FCSTD DOCUMENT  (FreeCAD 0.19RUnknown)
Label: Case-3RF-1DC
License: All rights reserved
LicenseURL: http://en.wikipedia.org/wiki/All_rights_reserved
objects: Part::FeaturePython×54, App::Part×36, Part::Feature×33, Sketcher::SketchObject×20, PartDesign::Boolean×13, PartDesign::Pocket×10, PartDesign::Pad×8, PartDesign::Body×3, PartDesign::AdditiveLoft×1
note: 161 computed .brp shape members not serialized (recipe doc carries the construction recipe); baked Part::Feature solids carry a one-line shape summary decoded from their .brp

FEATURE [Part::Feature] Part__Feature  label="SOLID"
  shape: bbox 3 x 3 x 0.52 mm, 110 faces (baked)
FEATURE [App::Part] UQFN_16_1EP_3x3mm_P0_5mm_EP1_75x1_75mm  label="UQFN-16-1EP_3x3mm_P0.5mm_EP1.75x1.75mm"
  Group = -> [Part__Feature]
  Origin = -> Origin
  Placement = pos=(150,-94,1.65) rot=(0,0,1;0rad)
FEATURE [Part::Feature] Part__Feature001  label="COMPOUND"
  shape: bbox 6.008 x 15.88 x 9.525 mm, 27 faces (baked)
FEATURE [Part::Feature] Part__Feature002  label="COMPOUND001"
  shape: bbox 2.61 x 2.61 x 7.92 mm, 9 faces (baked)
FEATURE [App::Part] COMPOUND  label="COMPOUND002"
  Group = -> [Part__Feature001,Part__Feature002]
  Origin = -> Origin001
FEATURE [App::Part] _42_1701_626  label="142-1701-626"
  Group = -> [COMPOUND]
  Origin = -> Origin002
  Placement = pos=(166.9,-93.75,1.85) rot=(0,1,0;1.5708rad)
FEATURE [Part::Feature] Part__Feature003  label="COMPOUND003"
  shape: bbox 6.008 x 15.88 x 9.525 mm, 27 faces (baked)
FEATURE [Part::Feature] Part__Feature004  label="COMPOUND004"
  shape: bbox 2.61 x 2.61 x 7.92 mm, 9 faces (baked)
FEATURE [App::Part] COMPOUND001  label="COMPOUND005"
  Group = -> [Part__Feature003,Part__Feature004]
  Origin = -> Origin003
FEATURE [App::Part] _42_1701_626001  label="142-1701-627"
  Group = -> [COMPOUND001]
  Origin = -> Origin004
  Placement = pos=(133.1,-93.75,1.85) rot=(-0.707107,0,0.707107;3.14159rad)
FEATURE [Part::Feature] Part__Feature005  label="COMPOUND006"
  shape: bbox 6.008 x 16 x 16.53 mm, 35 faces (baked)
FEATURE [App::Part] _32147_48  label="132147-48"
  Group = -> [Part__Feature005]
  Origin = -> Origin005
  Placement = pos=(150,-74.95,2.25) rot=(-0.57735,0.57735,0.57735;2.0944rad)
FEATURE [Part::Feature] Part__Feature006  label="SOLID001"
  shape: bbox 1 x 0.5 x 0.5 mm, 28 faces (baked)
FEATURE [App::Part] C_0402_1005Metric
  Group = -> [Part__Feature006]
  Origin = -> Origin006
  Placement = pos=(155.685,-89.7,1.65) rot=(0,0,1;0rad)
FEATURE [Part::Feature] Part__Feature007  label="SOLID002"
  shape: bbox 1 x 0.5 x 0.5 mm, 28 faces (baked)
FEATURE [App::Part] C_0402_1005Metric001
  Group = -> [Part__Feature007]
  Origin = -> Origin007
  Placement = pos=(155.685,-88.7,1.65) rot=(0,0,1;0rad)
FEATURE [Part::Feature] Part__Feature008  label="SOLID003"
  shape: bbox 1 x 0.5 x 0.5 mm, 28 faces (baked)
FEATURE [App::Part] C_0402_1005Metric002
  Group = -> [Part__Feature008]
  Origin = -> Origin008
  Placement = pos=(149.735,-88.175,1.65) rot=(0,0,1;0rad)
FEATURE [Part::Feature] Part__Feature009  label="SOLID004"
  shape: bbox 1 x 0.5 x 0.5 mm, 28 faces (baked)
FEATURE [App::Part] C_0402_1005Metric003
  Group = -> [Part__Feature009]
  Origin = -> Origin009
  Placement = pos=(149.735,-89.25,1.65) rot=(0,0,1;0rad)
FEATURE [Part::Feature] Part__Feature010  label="SOLID005"
  shape: bbox 1.6 x 0.8 x 0.8 mm, 28 faces (baked)
FEATURE [App::Part] C_0603_1608Metric
  Group = -> [Part__Feature010]
  Origin = -> Origin010
  Placement = pos=(154.787,-85.5,1.65) rot=(0,0,1;0rad)
FEATURE [Part::Feature] Part__Feature011  label="SOLID006"
  shape: bbox 1 x 0.5 x 0.5 mm, 28 faces (baked)
FEATURE [App::Part] L_0402_1005Metric
  Group = -> [Part__Feature011]
  Origin = -> Origin011
  Placement = pos=(149.25,-90.79,1.65) rot=(0,0,1;1.5708rad)
FEATURE [Part::Feature] Part__Feature012  label="SOLID007"
  shape: bbox 1.6 x 0.8 x 0.8 mm, 28 faces (baked)
FEATURE [App::Part] L_0603_1608Metric
  Group = -> [Part__Feature012]
  Origin = -> Origin012
  Placement = pos=(152.988,-91,1.65) rot=(0,0,1;0rad)
FEATURE [Part::Feature] Part__Feature013  label="SOLID008"
  shape: bbox 1 x 0.5 x 0.35 mm, 26 faces (baked)
FEATURE [App::Part] R_0402_1005Metric
  Group = -> [Part__Feature013]
  Origin = -> Origin013
  Placement = pos=(155.2,-87.2,1.65) rot=(0,0,1;1.5708rad)
FEATURE [Part::Feature] Part__Feature014  label="SOLID009"
  shape: bbox 1 x 0.5 x 0.35 mm, 26 faces (baked)
FEATURE [App::Part] R_0402_1005Metric001
  Group = -> [Part__Feature014]
  Origin = -> Origin014
  Placement = pos=(149.25,-86.65,1.65) rot=(0,0,-1;1.5708rad)
FEATURE [Part::Feature] Part__Feature015  label="SOLID010"
  shape: bbox 1 x 0.5 x 0.5 mm, 28 faces (baked)
FEATURE [App::Part] C_0402_1005Metric004
  Group = -> [Part__Feature015]
  Origin = -> Origin015
  Placement = pos=(158.265,-93.75,1.65) rot=(0,0,1;0rad)
FEATURE [Part::Feature] Part__Feature016  label="SOLID011"
  shape: bbox 1 x 0.5 x 0.35 mm, 26 faces (baked)
FEATURE [App::Part] R_0402_1005Metric002
  Group = -> [Part__Feature016]
  Origin = -> Origin016
  Placement = pos=(153.155,-93.75,1.65) rot=(0,0,1;3.14159rad)
FEATURE [Part::Feature] Part__Feature017  label="SOLID012"
  shape: bbox 1 x 0.5 x 0.35 mm, 26 faces (baked)
FEATURE [App::Part] R_0402_1005Metric003
  Group = -> [Part__Feature017]
  Origin = -> Origin017
  Placement = pos=(154.57,-94.235,1.65) rot=(0,0,1;1.5708rad)
FEATURE [Part::Feature] Part__Feature018  label="SOLID013"
  shape: bbox 1 x 0.5 x 0.5 mm, 28 faces (baked)
FEATURE [App::Part] C_0402_1005Metric005
  Group = -> [Part__Feature018]
  Origin = -> Origin018
  Placement = pos=(142.63,-94.235,1.65) rot=(0,0,1;1.5708rad)
FEATURE [Part::Feature] Part__Feature019  label="SOLID014"
  shape: bbox 1 x 0.5 x 0.5 mm, 28 faces (baked)
FEATURE [App::Part] C_0402_1005Metric006
  Group = -> [Part__Feature019]
  Origin = -> Origin019
  Placement = pos=(146.835,-93.75,1.65) rot=(0,0,1;0rad)
FEATURE [Part::Feature] Part__Feature020  label="SOLID015"
  shape: bbox 1 x 0.5 x 0.5 mm, 28 faces (baked)
FEATURE [App::Part] L_0402_1005Metric001
  Group = -> [Part__Feature020]
  Origin = -> Origin020
  Placement = pos=(144.03,-93.75,1.65) rot=(0,0,1;3.14159rad)
FEATURE [Part::Feature] Part__Feature021  label="SOLID016"
  shape: bbox 1 x 0.5 x 0.5 mm, 28 faces (baked)
FEATURE [App::Part] L_0402_1005Metric002
  Group = -> [Part__Feature021]
  Origin = -> Origin021
  Placement = pos=(145.43,-94.235,1.65) rot=(0,0,-1;1.5708rad)
FEATURE [Part::Feature] Part__Feature022  label="COMPOUND007"
  shape: bbox 30 x 30 x 1.6 mm, 14 faces (baked)
FEATURE [App::Part] Open_CASCADE_STEP_translator_6_9_1  label="Open CASCADE STEP translator 6.9 1"
  Group = -> [UQFN_16_1EP_3x3mm_P0_5mm_EP1_75x1_75mm,_42_1701_626,_42_1701_626001,_32147_48,C_0402_1005Metric,C_0402_1005Metric001,C_0402_1005Metric002,C_0402_1005Metric003,C_0603_1608Metric,L_0402_1005Metric,L_0603_1608Metric,R_0402_1005Metric,R_0402_1005Metric001,C_0402_1005Metric004,R_0402_1005Metric002,R_0402_1005Metric003,C_0402_1005Metric005,C_0402_1005Metric006,L_0402_1005Metric001,L_0402_1005Metric002,+1 more]
  Origin = -> Origin022
  Placement = pos=(-139,83,0) rot=(0,0,1;0rad)
FEATURE [Sketcher::SketchObject] Sketch
  FullyConstrained = true
  MapMode = 5
  Support = -> [XY_Plane023]
  sketch-geometry (32):
    g0: LineSegment StartX=23 StartY=8.05 StartZ=0 EndX=-1 EndY=8.05 EndZ=0
    g1: LineSegment StartX=-5.85 StartY=1 StartZ=0 EndX=-5.85 EndY=-23 EndZ=0
    g2: LineSegment StartX=-1 StartY=-27.85 StartZ=0 EndX=23 EndY=-27.85 EndZ=0
    g3: LineSegment StartX=27.85 StartY=-23 StartZ=0 EndX=27.85 EndY=1 EndZ=0
    g4: ArcOfCircle CenterX=23 CenterY=10.05 CenterZ=0 NormalX=0 NormalY=0 NormalZ=1 AngleXU=0 Radius=2 StartAngle=4.71239 EndAngle=6.28319
    g5: ArcOfCircle CenterX=29.85 CenterY=1 CenterZ=0 NormalX=0 NormalY=0 NormalZ=1 AngleXU=0 Radius=2 StartAngle=1.5708 EndAngle=3.14159
    g6: ArcOfCircle CenterX=-7.85 CenterY=-23 CenterZ=0 NormalX=0 NormalY=0 NormalZ=1 AngleXU=0 Radius=2 StartAngle=4.71239 EndAngle=6.28319
    g7: ArcOfCircle CenterX=-1 CenterY=-29.85 CenterZ=0 NormalX=0 NormalY=0 NormalZ=1 AngleXU=0 Radius=2 StartAngle=1.5708 EndAngle=3.14159
    g8: ArcOfCircle CenterX=23 CenterY=-29.85 CenterZ=0 NormalX=0 NormalY=0 NormalZ=1 AngleXU=0 Radius=2 StartAngle=0 EndAngle=1.5708
    g9: ArcOfCircle CenterX=29.85 CenterY=-23 CenterZ=0 NormalX=0 NormalY=0 NormalZ=1 AngleXU=0 Radius=2 StartAngle=3.14159 EndAngle=4.71239
    g10: ArcOfCircle CenterX=-1 CenterY=10.05 CenterZ=0 NormalX=0 NormalY=0 NormalZ=1 AngleXU=0 Radius=2 StartAngle=3.14159 EndAngle=4.71239
    g11: ArcOfCircle CenterX=-7.85 CenterY=1 CenterZ=0 NormalX=0 NormalY=0 NormalZ=1 AngleXU=0 Radius=2 StartAngle=0 EndAngle=1.5708
    g12: LineSegment StartX=25 StartY=10.05 StartZ=0 EndX=25 EndY=16 EndZ=0
    g13: LineSegment StartX=25 StartY=16 StartZ=0 EndX=38 EndY=16 EndZ=0
    g14: LineSegment StartX=38 StartY=16 StartZ=0 EndX=38 EndY=3 EndZ=0
    g15: LineSegment StartX=29.85 StartY=3 StartZ=0 EndX=38 EndY=3 EndZ=0
    g16: LineSegment StartX=-7.85 StartY=-25 StartZ=0 EndX=-16 EndY=-25 EndZ=0
    g17: LineSegment StartX=-16 StartY=-25 StartZ=0 EndX=-16 EndY=-38 EndZ=0
    g18: LineSegment StartX=-16 StartY=-38 StartZ=0 EndX=-3 EndY=-38 EndZ=0
    g19: LineSegment StartX=-3 StartY=-29.85 StartZ=0 EndX=-3 EndY=-38 EndZ=0
    g20: LineSegment StartX=29.85 StartY=-25 StartZ=0 EndX=38 EndY=-25 EndZ=0
    g21: LineSegment StartX=38 StartY=-25 StartZ=0 EndX=38 EndY=-38 EndZ=0
    g22: LineSegment StartX=38 StartY=-38 StartZ=0 EndX=25 EndY=-38 EndZ=0
    g23: LineSegment StartX=25 StartY=-38 StartZ=0 EndX=25 EndY=-29.85 EndZ=0
    g24: LineSegment StartX=-3 StartY=10.05 StartZ=0 EndX=-3 EndY=16 EndZ=0
    g25: LineSegment StartX=-3 StartY=16 StartZ=0 EndX=-16 EndY=16 EndZ=0
    g26: LineSegment StartX=-16 StartY=16 StartZ=0 EndX=-16 EndY=3 EndZ=0
    g27: LineSegment StartX=-7.85 StartY=3 StartZ=0 EndX=-16 EndY=3 EndZ=0
    g28: GeomPoint X=31.5 Y=9.5 Z=0
    g29: GeomPoint X=-9.5 Y=9.5 Z=0
    g30: GeomPoint X=-9.5 Y=-32.5 Z=0
    g31: GeomPoint X=31.5 Y=-32.5 Z=0
  constraints (98):
    c: Horizontal(g0)
    c: Horizontal(g2)
    c: Vertical(g1)
    c: Vertical(g3)
    c: Equal(g6,g7)
    c: Equal(g7,g8)
    c: Equal(g8,g9)
    c: Equal(g9,g5)
    c: Equal(g5,g4)
    c: Equal(g4,g10)
    c: Equal(g10,g11)
    c: Vertical(g8,g8)
    c: Vertical(g8,g4)
    c: Vertical(g4,g4)
    c: Horizontal(g9,g9)
    c: Horizontal(g9,g6)
    c: Horizontal(g6,g6)
    c: Horizontal(g11,g11)
    c: Horizontal(g11,g5)
    c: Horizontal(g5,g5)
    c: Vertical(g10,g10)
    c: Vertical(g10,g7)
    c: Vertical(g7,g7)
    c: Coincident(g0,g10)
    c: Coincident(g2,g7)
    c: Coincident(g6,g1)
    c: Horizontal(g7,g7)
    c: Horizontal(g8,g8)
    c: Coincident(g9,g3)
    c: Vertical(g6,g6)
    c: Vertical(g11,g11)
    c: Vertical(g9,g9)
    c: Vertical(g5,g5)
    c: Coincident(g0,g4)
    c: Horizontal(g10,g10)
    c: Horizontal(g4,g4)
    c: Coincident(g5,g3)
    c: Coincident(g1,g11)
    c: Coincident(g12,g4)
    c: Vertical(g12)
    c: Coincident(g13,g12)
    c: Horizontal(g13)
    c: Coincident(g14,g13)
    c: Vertical(g14)
    c: Coincident(g15,g5)
    c: Coincident(g15,g14)
    c: Horizontal(g15)
    c: Equal(g13,g14)
    c: DistanceX(g13,g13) = 13
    c: Coincident(g16,g6)
    c: Horizontal(g16)
    c: Coincident(g17,g16)
    c: Vertical(g17)
    c: Coincident(g18,g17)
    c: Horizontal(g18)
    c: Coincident(g19,g7)
    c: Coincident(g19,g18)
    c: Vertical(g19)
    c: Equal(g17,g18)
    c: Equal(g18,g14)
    c: Equal(g16,g19)
    c: Equal(g19,g15)
    c: Coincident(g20,g9)
    c: Horizontal(g20)
    c: Coincident(g21,g20)
    c: Vertical(g21)
    c: Coincident(g22,g21)
    c: Horizontal(g22)
    c: Coincident(g23,g22)
    c: Coincident(g23,g8)
    c: Vertical(g23)
    c: Equal(g14,g21)
    c: Equal(g21,g22)
    c: Coincident(g24,g10)
    c: Vertical(g24)
    c: Coincident(g25,g24)
    c: Horizontal(g25)
    c: Coincident(g26,g25)
    c: Vertical(g26)
    c: Coincident(g27,g11)
    c: Coincident(g27,g26)
    c: Horizontal(g27)
    c: DistanceX(g0,g0) = 24
    c: DistanceX(g1,g-1) = 5.85
    c: Radius(g10) = 2
    c: Coincident(g2,g8)
    c: DistanceX(g-1,g0) = -1
    c: DistanceY(g2,g-1) = 27.85
    c: DistanceY(g-1,g0) = 8.05
    c: Horizontal(g13,g25)
    c: Vertical(g25,g17)
    c: Horizontal(g31,g30)
    c: Vertical(g29,g30)
    c: Vertical(g28,g31)
    c: Symmetric(g14,g12,g28)
    c: Symmetric(g24,g26,g29)
    c: DistanceY(g30,g6) = 7.5
    c: Equal(g0,g1)
FEATURE [Sketcher::SketchObject] Sketch006
  AttachmentOffset = pos=(0,0,7) rot=(0,0,1;0rad)
  ExternalGeometry = -> [Sketch]
  FullyConstrained = true
  MapMode = 2
  sketch-geometry (36):
    g0: ArcOfCircle CenterX=22 CenterY=-1.4e-15 CenterZ=0 NormalX=0 NormalY=0 NormalZ=1 AngleXU=0 Radius=4.2 StartAngle=0 EndAngle=1.5708
    g1: ArcOfCircle CenterX=-1.54e-14 CenterY=0 CenterZ=0 NormalX=0 NormalY=0 NormalZ=1 AngleXU=0 Radius=4.2 StartAngle=1.5708 EndAngle=3.14159
    g2: ArcOfCircle CenterX=-1.54e-14 CenterY=-22 CenterZ=0 NormalX=0 NormalY=0 NormalZ=1 AngleXU=0 Radius=4.2 StartAngle=3.14159 EndAngle=4.71239
    g3: ArcOfCircle CenterX=22 CenterY=-22 CenterZ=0 NormalX=0 NormalY=0 NormalZ=1 AngleXU=0 Radius=4.2 StartAngle=4.71239 EndAngle=6.28319
    g4: LineSegment StartX=-1.54e-14 StartY=4.2 StartZ=0 EndX=22 EndY=4.2 EndZ=0
    g5: LineSegment StartX=26.2 StartY=-1.4e-15 StartZ=0 EndX=26.2 EndY=-22 EndZ=0
    g6: LineSegment StartX=-4.2 StartY=-1.4e-15 StartZ=0 EndX=-4.2 EndY=-22 EndZ=0
    g7: LineSegment StartX=-1.54e-14 StartY=-26.2 StartZ=0 EndX=22 EndY=-26.2 EndZ=0
    g8: LineSegment StartX=27.85 StartY=1 StartZ=0 EndX=27.85 EndY=-23 EndZ=0
    g9: LineSegment StartX=23 StartY=-27.85 StartZ=0 EndX=-1 EndY=-27.85 EndZ=0
    g10: LineSegment StartX=-3 StartY=-38 StartZ=0 EndX=-16 EndY=-38 EndZ=0
    g11: LineSegment StartX=-16 StartY=-38 StartZ=0 EndX=-16 EndY=-25 EndZ=0
    g12: LineSegment StartX=-5.85 StartY=-23 StartZ=0 EndX=-5.85 EndY=1 EndZ=0
    g13: LineSegment StartX=-1 StartY=8.05 StartZ=0 EndX=23 EndY=8.05 EndZ=0
    g14: ArcOfCircle CenterX=29.85 CenterY=1 CenterZ=0 NormalX=0 NormalY=0 NormalZ=1 AngleXU=0 Radius=2 StartAngle=1.5708 EndAngle=3.14159
    g15: ArcOfCircle CenterX=23 CenterY=10.05 CenterZ=0 NormalX=0 NormalY=0 NormalZ=1 AngleXU=0 Radius=2 StartAngle=4.71239 EndAngle=6.28319
    g16: ArcOfCircle CenterX=-1 CenterY=10.05 CenterZ=0 NormalX=0 NormalY=0 NormalZ=1 AngleXU=0 Radius=2 StartAngle=3.14159 EndAngle=4.71239
    g17: ArcOfCircle CenterX=-7.85 CenterY=1 CenterZ=0 NormalX=0 NormalY=0 NormalZ=1 AngleXU=0 Radius=2 StartAngle=0 EndAngle=1.5708
    g18: ArcOfCircle CenterX=-7.85 CenterY=-23 CenterZ=0 NormalX=0 NormalY=0 NormalZ=1 AngleXU=0 Radius=2 StartAngle=4.71239 EndAngle=6.28319
    g19: ArcOfCircle CenterX=29.85 CenterY=-23 CenterZ=0 NormalX=0 NormalY=0 NormalZ=1 AngleXU=0 Radius=2 StartAngle=3.14159 EndAngle=4.71239
    g20: ArcOfCircle CenterX=23 CenterY=-29.85 CenterZ=0 NormalX=0 NormalY=0 NormalZ=1 AngleXU=0 Radius=2 StartAngle=-1.013e-13 EndAngle=1.5708
    g21: ArcOfCircle CenterX=-1 CenterY=-29.85 CenterZ=0 NormalX=0 NormalY=0 NormalZ=1 AngleXU=0 Radius=2 StartAngle=1.5708 EndAngle=3.14159
    g22: LineSegment StartX=25 StartY=16 StartZ=0 EndX=38 EndY=16 EndZ=0
    g23: LineSegment StartX=38 StartY=16 StartZ=0 EndX=38 EndY=3 EndZ=0
    g24: LineSegment StartX=38 StartY=3 StartZ=0 EndX=29.85 EndY=3 EndZ=0
    g25: LineSegment StartX=25 StartY=10.05 StartZ=0 EndX=25 EndY=16 EndZ=0
    g26: LineSegment StartX=-3 StartY=10.05 StartZ=0 EndX=-3 EndY=16 EndZ=0
    g27: LineSegment StartX=-3 StartY=16 StartZ=0 EndX=-16 EndY=16 EndZ=0
    g28: LineSegment StartX=-16 StartY=16 StartZ=0 EndX=-16 EndY=3 EndZ=0
    g29: LineSegment StartX=-16 StartY=3 StartZ=0 EndX=-7.85 EndY=3 EndZ=0
    g30: LineSegment StartX=-16 StartY=-25 StartZ=0 EndX=-7.85 EndY=-25 EndZ=0
    g31: LineSegment StartX=-3 StartY=-38 StartZ=0 EndX=-3 EndY=-29.85 EndZ=0
    g32: LineSegment StartX=25 StartY=-29.85 StartZ=0 EndX=25 EndY=-38 EndZ=0
    g33: LineSegment StartX=25 StartY=-38 StartZ=0 EndX=38 EndY=-38 EndZ=0
    g34: LineSegment StartX=38 StartY=-38 StartZ=0 EndX=38 EndY=-25 EndZ=0
    g35: LineSegment StartX=38 StartY=-25 StartZ=0 EndX=29.85 EndY=-25 EndZ=0
  constraints (96):
    c: Coincident(g5,g0)
    c: Coincident(g5,g3)
    c: Vertical(g5)
    c: Coincident(g6,g1)
    c: Coincident(g6,g2)
    c: Vertical(g6)
    c: Coincident(g7,g2)
    c: Coincident(g7,g3)
    c: Horizontal(g7)
    c: Radius(g1) = 4.2
    c: Horizontal(g0,g0)
    c: Horizontal(g0,g1)
    c: Vertical(g0,g0)
    c: Vertical(g0,g3)
    c: Vertical(g3,g3)
    c: Vertical(g2,g2)
    c: Vertical(g2,g1)
    c: Coincident(g4,g1)
    c: Horizontal(g4)
    c: Coincident(g0,g4)
    c: DistanceX(g1,g0) = 22
    c: DistanceY(g3,g0) = 22
    c: Horizontal(g2,g2)
    c: Equal(g3,g2)
    c: Equal(g2,g0)
    c: Coincident(g1,g-1)
    c: Coincident(g11,g10)
    c: Coincident(g14,g8)
    c: Coincident(g15,g13)
    c: Coincident(g16,g13)
    c: Coincident(g17,g12)
    c: Coincident(g18,g12)
    c: Coincident(g19,g8)
    c: Coincident(g20,g9)
    c: Coincident(g21,g9)
    c: Coincident(g23,g22)
    c: Coincident(g24,g23)
    c: Coincident(g24,g14)
    c: Coincident(g25,g15)
    c: Coincident(g25,g22)
    c: Coincident(g26,g16)
    c: Coincident(g27,g26)
    c: Coincident(g28,g27)
    c: Coincident(g29,g28)
    c: Coincident(g29,g17)
    c: Coincident(g30,g11)
    c: Coincident(g30,g18)
    c: Coincident(g31,g10)
    c: Coincident(g31,g21)
    c: Coincident(g32,g20)
    c: Coincident(g33,g32)
    c: Coincident(g34,g33)
    c: Coincident(g35,g34)
    c: Coincident(g35,g19)
    c: Vertical(g1,g1)
    c: Coincident(g9,g-22)
    c: Coincident(g21,g-19)
    c: Coincident(g-18,g10)
    c: Equal(g-19,g21)
    c: Coincident(g20,g-20)
    c: Coincident(g9,g-22)
    c: Coincident(g20,g-21)
    c: Horizontal(g-21,g20)
    c: Coincident(g32,g-21)
    c: Coincident(g34,g-5)
    c: Coincident(g19,g-9)
    c: Horizontal(g8,g-9)
    c: Coincident(g19,g-9)
    c: Coincident(g14,g-8)
    c: Coincident(g23,g-6)
    c: Horizontal(g8,g14)
    c: Coincident(g14,g-8)
    c: Coincident(g15,g-17)
    c: Coincident(g22,g-17)
    c: Coincident(g-16,g15)
    c: Vertical(g13,g15)
    c: Coincident(g16,g-14)
    c: Coincident(g26,g-13)
    c: Coincident(g16,g-14)
    c: Vertical(g13,g16)
    c: Coincident(g28,g-3)
    c: Coincident(g17,g-11)
    c: Horizontal(g12,g-11)
    c: Coincident(g17,g-11)
    c: Coincident(g18,g-10)
    c: Coincident(g12,g-12)
    c: Vertical(g18,g18)
    c: Coincident(g11,g-4)
    c: Vertical(g28)
    c: Vertical(g11)
    c: Horizontal(g10)
    c: Horizontal(g33)
    c: Vertical(g34)
    c: Vertical(g23)
    c: Horizontal(g22)
    c: Horizontal(g27)
FEATURE [PartDesign::Pad] Pad
  Direction = (1,1,1)
  Length = 5
  Length2 = 100
  Profile = -> Sketch
  Reversed = true
  Type = 0
FEATURE [PartDesign::Pad] Pad001
  BaseFeature = -> Pad
  Direction = (1,1,1)
  Length = 9
  Length2 = 100
  Profile = -> Sketch006
  Type = 0
FEATURE [Sketcher::SketchObject] Sketch007
  AttachmentOffset = pos=(0,0,8.5) rot=(0,0,1;0rad)
  ExternalGeometry = -> [Sketch,Sketch006]
  FullyConstrained = true
  MapMode = 5
  Placement = pos=(0,0,8.5) rot=(0,0,1;0rad)
  Support = -> [XY_Plane023]
  sketch-geometry (12):
    g0: LineSegment StartX=38 StartY=16 StartZ=0 EndX=-16 EndY=16 EndZ=0
    g1: LineSegment StartX=-16 StartY=16 StartZ=0 EndX=-16 EndY=-38 EndZ=0
    g2: LineSegment StartX=-16 StartY=-38 StartZ=0 EndX=38 EndY=-38 EndZ=0
    g3: LineSegment StartX=38 StartY=-38 StartZ=0 EndX=38 EndY=16 EndZ=0
    g4: ArcOfCircle CenterX=22 CenterY=-22 CenterZ=0 NormalX=0 NormalY=0 NormalZ=1 AngleXU=0 Radius=4.2 StartAngle=4.71239 EndAngle=6.28319
    g5: ArcOfCircle CenterX=22 CenterY=-6e-16 CenterZ=0 NormalX=0 NormalY=0 NormalZ=1 AngleXU=0 Radius=4.2 StartAngle=0 EndAngle=1.5708
    g6: ArcOfCircle CenterX=0 CenterY=0 CenterZ=0 NormalX=0 NormalY=0 NormalZ=1 AngleXU=0 Radius=4.2 StartAngle=1.5708 EndAngle=3.14159
    g7: ArcOfCircle CenterX=-8e-16 CenterY=-22 CenterZ=0 NormalX=0 NormalY=0 NormalZ=1 AngleXU=0 Radius=4.2 StartAngle=3.14159 EndAngle=4.71239
    g8: LineSegment StartX=22 StartY=4.2 StartZ=0 EndX=0 EndY=4.2 EndZ=0
    g9: LineSegment StartX=-4.2 StartY=-1.4e-15 StartZ=0 EndX=-4.2 EndY=-22 EndZ=0
    g10: LineSegment StartX=-1.6e-15 StartY=-26.2 StartZ=0 EndX=22 EndY=-26.2 EndZ=0
    g11: LineSegment StartX=26.2 StartY=-22 StartZ=0 EndX=26.2 EndY=0 EndZ=0
  constraints (30):
    c: Coincident(g0,g1)
    c: Coincident(g1,g2)
    c: Coincident(g2,g3)
    c: Coincident(g3,g0)
    c: Horizontal(g0)
    c: Horizontal(g2)
    c: Vertical(g1)
    c: Vertical(g3)
    c: Coincident(g0,g-3)
    c: Coincident(g1,g-5)
    c: Coincident(g4,g-10)
    c: Coincident(g4,g-10)
    c: Coincident(g4,g-10)
    c: Coincident(g5,g-7)
    c: Coincident(g5,g-7)
    c: Coincident(g5,g-7)
    c: Coincident(g6,g-1)
    c: Coincident(g6,g-9)
    c: Coincident(g6,g-9)
    c: Coincident(g7,g-8)
    c: Coincident(g7,g-8)
    c: Coincident(g7,g-8)
    c: Coincident(g8,g5)
    c: Coincident(g8,g6)
    c: Coincident(g9,g6)
    c: Coincident(g9,g7)
    c: Coincident(g10,g7)
    c: Coincident(g10,g4)
    c: Coincident(g11,g4)
    c: Coincident(g11,g5)
FEATURE [PartDesign::Pad] Pad002
  BaseFeature = -> Pad001
  Direction = (1,1,1)
  Length = 3.5
  Length2 = 100
  Profile = -> Sketch007
  Type = 0
FEATURE [Sketcher::SketchObject] Sketch008
  AttachmentOffset = pos=(0,0,12) rot=(0,0,1;0rad)
  ExternalGeometry = -> [Sketch007]
  FullyConstrained = true
  MapMode = 5
  Placement = pos=(0,0,12) rot=(0,0,1;0rad)
  Support = -> [XY_Plane023]
  sketch-geometry (16):
    g0: ArcOfCircle CenterX=22 CenterY=-6e-16 CenterZ=0 NormalX=0 NormalY=0 NormalZ=1 AngleXU=0 Radius=5.5 StartAngle=1e-16 EndAngle=1.5708
    g1: ArcOfCircle CenterX=22 CenterY=-6e-16 CenterZ=0 NormalX=0 NormalY=0 NormalZ=1 AngleXU=0 Radius=8.5 StartAngle=1e-16 EndAngle=1.5708
    g2: ArcOfCircle CenterX=0 CenterY=0 CenterZ=0 NormalX=0 NormalY=0 NormalZ=1 AngleXU=0 Radius=5.5 StartAngle=1.5708 EndAngle=3.14159
    g3: ArcOfCircle CenterX=0 CenterY=0 CenterZ=0 NormalX=0 NormalY=0 NormalZ=1 AngleXU=0 Radius=8.5 StartAngle=1.5708 EndAngle=3.14159
    g4: LineSegment StartX=5e-16 StartY=8.5 StartZ=0 EndX=22 EndY=8.5 EndZ=0
    g5: LineSegment StartX=3e-16 StartY=5.5 StartZ=0 EndX=22 EndY=5.5 EndZ=0
    g6: ArcOfCircle CenterX=22 CenterY=-22 CenterZ=0 NormalX=0 NormalY=0 NormalZ=1 AngleXU=0 Radius=5.5 StartAngle=4.71239 EndAngle=6.28319
    g7: ArcOfCircle CenterX=22 CenterY=-22 CenterZ=0 NormalX=0 NormalY=0 NormalZ=1 AngleXU=0 Radius=8.5 StartAngle=4.71239 EndAngle=6.28319
    g8: ArcOfCircle CenterX=-5.8e-15 CenterY=-22 CenterZ=0 NormalX=0 NormalY=0 NormalZ=1 AngleXU=0 Radius=5.5 StartAngle=3.14159 EndAngle=4.71239
    g9: ArcOfCircle CenterX=-5.8e-15 CenterY=-22 CenterZ=0 NormalX=0 NormalY=0 NormalZ=1 AngleXU=0 Radius=8.5 StartAngle=3.14159 EndAngle=4.71239
    g10: LineSegment StartX=-5.5 StartY=-22 StartZ=0 EndX=-5.5 EndY=0 EndZ=0
    g11: LineSegment StartX=-8.5 StartY=1e-15 StartZ=0 EndX=-8.5 EndY=-22 EndZ=0
    g12: LineSegment StartX=-5.8e-15 StartY=-27.5 StartZ=0 EndX=22 EndY=-27.5 EndZ=0
    g13: LineSegment StartX=-7.4e-15 StartY=-30.5 StartZ=0 EndX=22 EndY=-30.5 EndZ=0
    g14: LineSegment StartX=27.5 StartY=-22 StartZ=0 EndX=27.5 EndY=0 EndZ=0
    g15: LineSegment StartX=30.5 StartY=3e-16 StartZ=0 EndX=30.5 EndY=-22 EndZ=0
  constraints (49):
    c: Coincident(g0,g-7)
    c: PointOnObject(g0,g-1)
    c: Coincident(g1,g0)
    c: PointOnObject(g1,g-1)
    c: PointOnObject(g2,g-2)
    c: PointOnObject(g2,g-1)
    c: PointOnObject(g3,g-2)
    c: PointOnObject(g3,g-1)
    c: Coincident(g4,g3)
    c: Coincident(g4,g1)
    c: Horizontal(g4)
    c: Tangent(g4,g1)
    c: Coincident(g5,g2)
    c: Coincident(g5,g0)
    c: Horizontal(g5)
    c: Coincident(g6,g-8)
    c: Coincident(g7,g6)
    c: PointOnObject(g9,g-2)
    c: Coincident(g10,g8)
    c: Coincident(g10,g2)
    c: Vertical(g10)
    c: Coincident(g11,g3)
    c: Coincident(g11,g9)
    c: Vertical(g11)
    c: Coincident(g12,g8)
    c: Coincident(g12,g6)
    c: Horizontal(g12)
    c: Coincident(g13,g9)
    c: Coincident(g13,g7)
    c: Horizontal(g13)
    c: Coincident(g14,g6)
    c: Coincident(g14,g0)
    c: Vertical(g14)
    c: Coincident(g15,g1)
    c: Coincident(g15,g7)
    c: Coincident(g3,g-1)
    c: Coincident(g2,g3)
    c: Vertical(g0,g1)
    c: Vertical(g6,g7)
    c: Vertical(g7,g6)
    c: Horizontal(g8,g9)
    c: Radius(g8) = 5.5
    c: Radius(g9) = 8.5
    c: Horizontal(g7,g6)
    c: Coincident(g8,g9)
    c: Coincident(g8,g-5)
    c: Vertical(g8,g8)
    c: Horizontal(g8,g8)
    c: DistanceX(g4,g4) = 22
FEATURE [PartDesign::Pocket] Pocket
  BaseFeature = -> Pad002
  Length = 2.8
  Length2 = 100
  Profile = -> Sketch008
  Type = 0
FEATURE [Part::FeaturePython] ScrewTap  label="M3x20.0-ScrewTap007"  # Fasteners workbench fastener (typed FeaturePython)
  Placement = pos=(0,0,10) rot=(0,0,1;0rad)
  diameter = 4
  invert = false
  length = 20
  matchOuter = true
  offset = 0
  thread = true
FEATURE [Part::FeaturePython] ScrewTap001  label="M3x20.0-ScrewTap006"  # Fasteners workbench fastener (typed FeaturePython)
  Placement = pos=(22,0,10) rot=(0,0,1;0rad)
  diameter = 4
  invert = false
  length = 20
  matchOuter = true
  offset = 0
  thread = true
FEATURE [Part::FeaturePython] ScrewTap002  label="M3x20.0-ScrewTap005"  # Fasteners workbench fastener (typed FeaturePython)
  Placement = pos=(22,-22,10) rot=(0,0,1;0rad)
  diameter = 4
  invert = false
  length = 20
  matchOuter = true
  offset = 0
  thread = true
FEATURE [Part::FeaturePython] ScrewTap003  label="M3x20.0-ScrewTap004"  # Fasteners workbench fastener (typed FeaturePython)
  Placement = pos=(0,-22,10) rot=(0,0,1;0rad)
  diameter = 4
  invert = false
  length = 20
  matchOuter = true
  offset = 0
  thread = true
FEATURE [Part::FeaturePython] ScrewTap004  label="M3x20.0-ScrewTap054"  # Fasteners workbench fastener (typed FeaturePython)
  Placement = pos=(-12,-34,12) rot=(0,0,1;0rad)
  diameter = 4
  invert = false
  length = 20
  matchOuter = true
  offset = 0
  thread = true
FEATURE [Part::FeaturePython] ScrewTap005  label="M3x20.0-ScrewTap055"  # Fasteners workbench fastener (typed FeaturePython)
  Placement = pos=(-12,12,12) rot=(0,0,1;0rad)
  diameter = 4
  invert = false
  length = 20
  matchOuter = true
  offset = 0
  thread = true
FEATURE [Part::FeaturePython] ScrewTap006  label="M3x20.0-ScrewTap056"  # Fasteners workbench fastener (typed FeaturePython)
  Placement = pos=(34,-34,12) rot=(0,0,1;0rad)
  diameter = 4
  invert = false
  length = 20
  matchOuter = true
  offset = 0
  thread = true
FEATURE [Part::FeaturePython] ScrewTap007  label="M3x20.0-ScrewTap"  # Fasteners workbench fastener (typed FeaturePython)
  Placement = pos=(34,12,12) rot=(0,0,1;0rad)
  diameter = 4
  invert = false
  length = 20
  matchOuter = true
  offset = 0
  thread = true
FEATURE [Part::FeaturePython] ScrewTap008  label="M2.5x20.0-ScrewTap"  # Fasteners workbench fastener (typed FeaturePython)
  Placement = pos=(4.9,-5,2.25) rot=(1,0,0;1.5708rad)
  diameter = 3
  invert = false
  length = 20
  matchOuter = true
  offset = 0
  thread = true
FEATURE [Part::FeaturePython] ScrewTap009  label="M2.5x50.0-ScrewTap"  # Fasteners workbench fastener (typed FeaturePython)
  Placement = pos=(36.1,-17.105,1.85) rot=(0,1,0;1.5708rad)
  diameter = 3
  invert = false
  length = 50
  matchOuter = true
  offset = 0
  thread = true
FEATURE [Part::FeaturePython] ScrewTap010  label="M2.5x20.0-ScrewTap001"  # Fasteners workbench fastener (typed FeaturePython)
  Placement = pos=(17.1,-5,2.25) rot=(1,0,0;1.5708rad)
  diameter = 3
  invert = false
  length = 20
  matchOuter = true
  offset = 0
  thread = true
FEATURE [Part::FeaturePython] ScrewTap011  label="M2.5x50.0-ScrewTap001"  # Fasteners workbench fastener (typed FeaturePython)
  Placement = pos=(36.1,-4.895,1.85) rot=(0,1,0;1.5708rad)
  diameter = 3
  invert = false
  length = 50
  matchOuter = true
  offset = 0
  thread = true
FEATURE [Part::FeaturePython] ScrewTap012  label="M2.5x20.0-ScrewTap002"  # Fasteners workbench fastener (typed FeaturePython)
  Placement = pos=(4.64,-37,1.85) rot=(1,0,0;1.5708rad)
  diameter = 3
  invert = false
  length = 20
  matchOuter = true
  offset = 0
  thread = true
FEATURE [Part::FeaturePython] ScrewTap013  label="M2.5x20.0-ScrewTap003"  # Fasteners workbench fastener (typed FeaturePython)
  Placement = pos=(16.86,-37,1.85) rot=(1,0,0;1.5708rad)
  diameter = 3
  invert = false
  length = 20
  matchOuter = true
  offset = 0
  thread = true
FEATURE [PartDesign::Boolean] Boolean
  BaseFeature = -> Pocket
  Group = -> [ScrewTap]
  Refine = true
  Type = 1
FEATURE [PartDesign::Boolean] Boolean001
  BaseFeature = -> Boolean
  Group = -> [ScrewTap001]
  Refine = true
  Type = 1
FEATURE [PartDesign::Boolean] Boolean002
  BaseFeature = -> Boolean001
  Group = -> [ScrewTap002]
  Refine = true
  Type = 1
FEATURE [PartDesign::Boolean] Boolean003
  BaseFeature = -> Boolean002
  Group = -> [ScrewTap003,ScrewTap004,ScrewTap005,ScrewTap006,ScrewTap007]
  Refine = true
  Type = 1
FEATURE [PartDesign::Boolean] Boolean004
  BaseFeature = -> Boolean003
  Group = -> [ScrewTap008,ScrewTap009,ScrewTap010,ScrewTap011,ScrewTap012,ScrewTap013]
  Refine = true
  Type = 1
FEATURE [Sketcher::SketchObject] Sketch009
  AttachmentOffset = pos=(0,0,28) rot=(0,0,1;0rad)
  FullyConstrained = true
  MapMode = 5
  Placement = pos=(28,-6.2e-15,6.2e-15) rot=(0.57735,0.57735,0.57735;2.0944rad)
  Support = -> [YZ_Plane023]
  sketch-geometry (1):
    g0: Circle CenterX=-11 CenterY=1.85 CenterZ=0 NormalX=0 NormalY=0 NormalZ=1 AngleXU=0 Radius=1.9
  constraints (3):
    c: DistanceY(g-1,g0) = 1.85
    c: Radius(g0) = 1.9
    c: DistanceX(g0,g-1) = 11
FEATURE [PartDesign::Pocket] Pocket001
  BaseFeature = -> Boolean004
  Length = 2
  Length2 = 100
  Profile = -> Sketch009
  Type = 0
FEATURE [Sketcher::SketchObject] Sketch010
  AttachmentOffset = pos=(0,0,28) rot=(0,0,1;0rad)
  FullyConstrained = true
  MapMode = 5
  Placement = pos=(0,-28,-6.2e-15) rot=(1,0,0;1.5708rad)
  Support = -> [XZ_Plane023]
  sketch-geometry (1):
    g0: Circle CenterX=11 CenterY=1.85 CenterZ=0 NormalX=0 NormalY=0 NormalZ=1 AngleXU=0 Radius=1.9
  constraints (3):
    c: DistanceX(g-1,g0) = 11
    c: DistanceY(g-1,g0) = 1.85
    c: Radius(g0) = 1.9
FEATURE [PartDesign::Pocket] Pocket002
  BaseFeature = -> Pocket001
  Length = 2
  Length2 = 100
  Profile = -> Sketch010
  Type = 0
FEATURE [Sketcher::SketchObject] Sketch011
  AttachmentOffset = pos=(0,0,-9) rot=(0,0,1;0rad)
  FullyConstrained = true
  MapMode = 5
  Placement = pos=(0,9,2e-15) rot=(1,0,0;1.5708rad)
  Support = -> [XZ_Plane023]
  sketch-geometry (1):
    g0: Circle CenterX=11 CenterY=2.25 CenterZ=0 NormalX=0 NormalY=0 NormalZ=1 AngleXU=0 Radius=1.9
  constraints (3):
    c: DistanceX(g-1,g0) = 11
    c: DistanceY(g-1,g0) = 2.25
    c: Radius(g0) = 1.9
FEATURE [PartDesign::Pocket] Pocket003
  BaseFeature = -> Pocket002
  Length = 5
  Length2 = 100
  Profile = -> Sketch011
  Reversed = true
  Type = 0
FEATURE [Sketcher::SketchObject] Sketch012
  AttachmentOffset = pos=(0,0,-6) rot=(0,0,1;0rad)
  ExternalGeometry = -> [Sketch009]
  FullyConstrained = true
  MapMode = 5
  Placement = pos=(-6,1.3e-15,-1.3e-15) rot=(0.57735,0.57735,0.57735;2.0944rad)
  Support = -> [YZ_Plane023]
  sketch-geometry (1):
    g0: Circle CenterX=-11 CenterY=1.85 CenterZ=0 NormalX=0 NormalY=0 NormalZ=1 AngleXU=0 Radius=1.9
  constraints (2):
    c: Coincident(g0,g-3)
    c: Tangent(g0,g-3)
FEATURE [PartDesign::Pocket] Pocket004
  BaseFeature = -> Pocket003
  Length = 2
  Length2 = 100
  Profile = -> Sketch012
  Reversed = true
  Type = 0
FEATURE [Sketcher::SketchObject] Sketch013
  AttachmentOffset = pos=(0,0,12) rot=(0,0,1;0rad)
  FullyConstrained = true
  MapMode = 5
  Placement = pos=(0,0,12) rot=(0,0,1;0rad)
  Support = -> [XY_Plane026]
  sketch-geometry (23):
    g0: LineSegment StartX=-16 StartY=16 StartZ=0 EndX=38 EndY=16 EndZ=0
    g1: LineSegment StartX=38 StartY=16 StartZ=0 EndX=38 EndY=-38 EndZ=0
    g2: LineSegment StartX=38 StartY=-38 StartZ=0 EndX=-16 EndY=-38 EndZ=0
    g3: LineSegment StartX=-16 StartY=-38 StartZ=0 EndX=-16 EndY=16 EndZ=0
    g4: GeomPoint X=22 Y=0 Z=0
    g5: GeomPoint X=22 Y=-22 Z=0
    g6: GeomPoint X=0 Y=-22 Z=0
    g7: Circle CenterX=-12 CenterY=12 CenterZ=0 NormalX=0 NormalY=0 NormalZ=1 AngleXU=0 Radius=1.75
    g8: Circle CenterX=34 CenterY=12 CenterZ=0 NormalX=0 NormalY=0 NormalZ=1 AngleXU=0 Radius=1.75
    g9: Circle CenterX=34 CenterY=-34 CenterZ=0 NormalX=0 NormalY=0 NormalZ=1 AngleXU=0 Radius=1.75
    g10: Circle CenterX=-12 CenterY=-34 CenterZ=0 NormalX=0 NormalY=0 NormalZ=1 AngleXU=0 Radius=1.75
    g11: Circle CenterX=34 CenterY=-11 CenterZ=0 NormalX=0 NormalY=0 NormalZ=1 AngleXU=0 Radius=1.75
    g12: Circle CenterX=34 CenterY=0.5 CenterZ=0 NormalX=0 NormalY=0 NormalZ=1 AngleXU=0 Radius=1.75
    g13: Circle CenterX=34 CenterY=-22.5 CenterZ=0 NormalX=0 NormalY=0 NormalZ=1 AngleXU=0 Radius=1.75
    g14: Circle CenterX=22.5 CenterY=-34 CenterZ=0 NormalX=0 NormalY=0 NormalZ=1 AngleXU=0 Radius=1.75
    g15: Circle CenterX=11 CenterY=-34 CenterZ=0 NormalX=0 NormalY=0 NormalZ=1 AngleXU=0 Radius=1.75
    g16: Circle CenterX=-0.5 CenterY=-34 CenterZ=0 NormalX=0 NormalY=0 NormalZ=1 AngleXU=0 Radius=1.75
    g17: Circle CenterX=-12 CenterY=-22.5 CenterZ=0 NormalX=0 NormalY=0 NormalZ=1 AngleXU=0 Radius=1.75
    g18: Circle CenterX=-12 CenterY=-11 CenterZ=0 NormalX=0 NormalY=0 NormalZ=1 AngleXU=0 Radius=1.75
    g19: Circle CenterX=-12 CenterY=0.5 CenterZ=0 NormalX=0 NormalY=0 NormalZ=1 AngleXU=0 Radius=1.75
    g20: Circle CenterX=11 CenterY=12 CenterZ=0 NormalX=0 NormalY=0 NormalZ=1 AngleXU=0 Radius=1.75
    g21: Circle CenterX=22.5 CenterY=12 CenterZ=0 NormalX=0 NormalY=0 NormalZ=1 AngleXU=0 Radius=1.75
    g22: Circle CenterX=-0.5 CenterY=12 CenterZ=0 NormalX=0 NormalY=0 NormalZ=1 AngleXU=0 Radius=1.75
  constraints (67):
    c: Coincident(g0,g1)
    c: Coincident(g1,g2)
    c: Coincident(g2,g3)
    c: Coincident(g3,g0)
    c: Horizontal(g0)
    c: Horizontal(g2)
    c: Vertical(g1)
    c: Vertical(g3)
    c: DistanceX(g0,g0) = 54
    c: DistanceY(g3,g3) = 54
    c: DistanceY(g-1,g0) = 16
    c: DistanceX(g0,g-1) = 16
    c: PointOnObject(g4,g-1)
    c: PointOnObject(g6,g-2)
    c: DistanceX(g-1,g4) = 22
    c: Vertical(g4,g5)
    c: Horizontal(g5,g6)
    c: DistanceY(g6,g-1) = 22
    c: Vertical(g10,g7)
    c: Vertical(g8,g9)
    c: Horizontal(g7,g8)
    c: Horizontal(g10,g9)
    c: DistanceX(g7,g-1) = 12
    c: DistanceY(g-1,g7) = 12
    c: Equal(g7,g8)
    c: Equal(g8,g9)
    c: Equal(g9,g10)
    c: Radius(g7) = 1.75
    c: DistanceX(g4,g8) = 12
    c: DistanceY(g10,g6) = 12
    c: DistanceX(g10,g9) = 46
    c: Vertical(g19,g7)
    c: Vertical(g7,g18)
    c: Vertical(g18,g17)
    c: Horizontal(g16,g15)
    c: Horizontal(g15,g14)
    c: Horizontal(g14,g9)
    c: Vertical(g11,g13)
    c: Vertical(g13,g12)
    c: Vertical(g12,g8)
    c: Horizontal(g22,g7)
    c: Horizontal(g7,g20)
    c: Horizontal(g20,g21)
    c: DistanceX(g21,g8) = 11.5
    c: DistanceX(g20,g21) = 11.5
    c: DistanceX(g22,g20) = 11.5
    c: Equal(g21,g20)
    c: Equal(g20,g22)
    c: Equal(g22,g7)
    c: Vertical(g16,g22)
    c: Vertical(g15,g20)
    c: Vertical(g14,g21)
    c: Equal(g14,g15)
    c: Equal(g15,g16)
    c: Equal(g16,g7)
    c: DistanceY(g12,g8) = 11.5
    c: DistanceY(g11,g12) = 11.5
    c: DistanceY(g13,g11) = 11.5
    c: Equal(g12,g11)
    c: Equal(g11,g13)
    c: Equal(g13,g8)
    c: Horizontal(g19,g12)
    c: Horizontal(g18,g11)
    c: Horizontal(g17,g13)
    c: Equal(g17,g18)
    c: Equal(g18,g19)
    c: Equal(g19,g7)
FEATURE [Sketcher::SketchObject] Sketch014
  AttachmentOffset = pos=(0,0,12) rot=(0,0,1;0rad)
  FullyConstrained = true
  MapMode = 5
  Placement = pos=(0,0,12) rot=(0,0,1;0rad)
  Support = -> [XY_Plane026]
  sketch-geometry (11):
    g0: GeomPoint X=22 Y=0 Z=0
    g1: GeomPoint X=0 Y=-22 Z=0
    g2: GeomPoint X=22 Y=-22 Z=0
    g3: ArcOfCircle CenterX=22 CenterY=0 CenterZ=0 NormalX=0 NormalY=0 NormalZ=1 AngleXU=0 Radius=1.2 StartAngle=0 EndAngle=1.5708
    g4: ArcOfCircle CenterX=22 CenterY=-22 CenterZ=0 NormalX=0 NormalY=0 NormalZ=1 AngleXU=0 Radius=1.2 StartAngle=4.71239 EndAngle=6.28319
    g5: ArcOfCircle CenterX=0 CenterY=-22 CenterZ=0 NormalX=0 NormalY=0 NormalZ=1 AngleXU=0 Radius=1.2 StartAngle=3.14159 EndAngle=4.71239
    g6: ArcOfCircle CenterX=0 CenterY=0 CenterZ=0 NormalX=0 NormalY=0 NormalZ=1 AngleXU=0 Radius=1.2 StartAngle=1.5708 EndAngle=3.14159
    g7: LineSegment StartX=-1.2 StartY=1e-16 StartZ=0 EndX=-1.2 EndY=-22 EndZ=0
    g8: LineSegment StartX=-2e-16 StartY=-23.2 StartZ=0 EndX=22 EndY=-23.2 EndZ=0
    g9: LineSegment StartX=23.2 StartY=-22 StartZ=0 EndX=23.2 EndY=0 EndZ=0
    g10: LineSegment StartX=22 StartY=1.2 StartZ=0 EndX=0 EndY=1.2 EndZ=0
  constraints (30):
    c: PointOnObject(g0,g-1)
    c: PointOnObject(g1,g-2)
    c: DistanceX(g-1,g0) = 22
    c: DistanceY(g1,g-1) = 22
    c: Vertical(g2,g0)
    c: Horizontal(g1,g2)
    c: Coincident(g3,g0)
    c: PointOnObject(g3,g-1)
    c: Coincident(g4,g2)
    c: Coincident(g5,g1)
    c: PointOnObject(g5,g-2)
    c: Coincident(g6,g-1)
    c: PointOnObject(g6,g-1)
    c: PointOnObject(g6,g-2)
    c: Equal(g6,g3)
    c: Equal(g3,g4)
    c: Equal(g4,g5)
    c: Coincident(g7,g6)
    c: Coincident(g7,g5)
    c: Vertical(g7)
    c: Coincident(g8,g5)
    c: Coincident(g8,g4)
    c: Horizontal(g8)
    c: Coincident(g9,g4)
    c: Coincident(g9,g3)
    c: Vertical(g9)
    c: Coincident(g10,g3)
    c: Coincident(g10,g6)
    c: Horizontal(g10)
    c: Radius(g6) = 1.2
FEATURE [Sketcher::SketchObject] Sketch015
  AttachmentOffset = pos=(0,0,9) rot=(0,0,1;0rad)
  FullyConstrained = true
  MapMode = 5
  Placement = pos=(0,0,7) rot=(0,0,1;0rad)
  sketch-geometry (11):
    g0: GeomPoint X=22 Y=0 Z=0
    g1: GeomPoint X=0 Y=-22 Z=0
    g2: GeomPoint X=22 Y=-22 Z=0
    g3: ArcOfCircle CenterX=22 CenterY=0 CenterZ=0 NormalX=0 NormalY=0 NormalZ=1 AngleXU=0 Radius=1.2 StartAngle=0 EndAngle=1.5708
    g4: ArcOfCircle CenterX=22 CenterY=-22 CenterZ=0 NormalX=0 NormalY=0 NormalZ=1 AngleXU=0 Radius=1.2 StartAngle=4.71239 EndAngle=6.28319
    g5: ArcOfCircle CenterX=0 CenterY=-22 CenterZ=0 NormalX=0 NormalY=0 NormalZ=1 AngleXU=0 Radius=1.2 StartAngle=3.14159 EndAngle=4.71239
    g6: ArcOfCircle CenterX=0 CenterY=0 CenterZ=0 NormalX=0 NormalY=0 NormalZ=1 AngleXU=0 Radius=1.2 StartAngle=1.5708 EndAngle=3.14159
    g7: LineSegment StartX=-1.2 StartY=1e-16 StartZ=0 EndX=-1.2 EndY=-22 EndZ=0
    g8: LineSegment StartX=-2e-16 StartY=-23.2 StartZ=0 EndX=22 EndY=-23.2 EndZ=0
    g9: LineSegment StartX=23.2 StartY=-22 StartZ=0 EndX=23.2 EndY=0 EndZ=0
    g10: LineSegment StartX=22 StartY=1.2 StartZ=0 EndX=0 EndY=1.2 EndZ=0
  constraints (30):
    c: PointOnObject(g0,g-1)
    c: PointOnObject(g1,g-2)
    c: DistanceX(g-1,g0) = 22
    c: DistanceY(g1,g-1) = 22
    c: Vertical(g2,g0)
    c: Horizontal(g1,g2)
    c: Coincident(g3,g0)
    c: PointOnObject(g3,g-1)
    c: Coincident(g4,g2)
    c: Coincident(g5,g1)
    c: PointOnObject(g5,g-2)
    c: Coincident(g6,g-1)
    c: PointOnObject(g6,g-1)
    c: PointOnObject(g6,g-2)
    c: Equal(g6,g3)
    c: Equal(g3,g4)
    c: Equal(g4,g5)
    c: Coincident(g7,g6)
    c: Coincident(g7,g5)
    c: Vertical(g7)
    c: Coincident(g8,g5)
    c: Coincident(g8,g4)
    c: Horizontal(g8)
    c: Coincident(g9,g4)
    c: Coincident(g9,g3)
    c: Vertical(g9)
    c: Coincident(g10,g3)
    c: Coincident(g10,g6)
    c: Horizontal(g10)
    c: Radius(g6) = 1.2
FEATURE [Sketcher::SketchObject] Sketch016
  AttachmentOffset = pos=(0,0,9) rot=(0,0,1;0rad)
  FullyConstrained = true
  MapMode = 5
  Placement = pos=(0,0,7) rot=(0,0,1;0rad)
  sketch-geometry (11):
    g0: GeomPoint X=22 Y=0 Z=0
    g1: GeomPoint X=0 Y=-22 Z=0
    g2: GeomPoint X=22 Y=-22 Z=0
    g3: ArcOfCircle CenterX=22 CenterY=0 CenterZ=0 NormalX=0 NormalY=0 NormalZ=1 AngleXU=0 Radius=4 StartAngle=0 EndAngle=1.57079
    g4: ArcOfCircle CenterX=22 CenterY=-22 CenterZ=0 NormalX=0 NormalY=0 NormalZ=1 AngleXU=0 Radius=4 StartAngle=4.7124 EndAngle=6.28318
    g5: ArcOfCircle CenterX=0 CenterY=-22 CenterZ=0 NormalX=0 NormalY=0 NormalZ=1 AngleXU=0 Radius=4 StartAngle=3.1416 EndAngle=4.71239
    g6: ArcOfCircle CenterX=0 CenterY=0 CenterZ=0 NormalX=0 NormalY=0 NormalZ=1 AngleXU=0 Radius=4 StartAngle=1.5708 EndAngle=3.14159
    g7: LineSegment StartX=-4 StartY=5e-16 StartZ=0 EndX=-4 EndY=-22 EndZ=0
    g8: LineSegment StartX=-7e-16 StartY=-26 StartZ=0 EndX=22 EndY=-26 EndZ=0
    g9: LineSegment StartX=26 StartY=-22 StartZ=0 EndX=26 EndY=0 EndZ=0
    g10: LineSegment StartX=22 StartY=4 StartZ=0 EndX=0 EndY=4 EndZ=0
  constraints (30):
    c: PointOnObject(g0,g-1)
    c: PointOnObject(g1,g-2)
    c: DistanceX(g-1,g0) = 22
    c: DistanceY(g1,g-1) = 22
    c: Vertical(g2,g0)
    c: Horizontal(g1,g2)
    c: Coincident(g3,g0)
    c: PointOnObject(g3,g-1)
    c: Coincident(g4,g2)
    c: Coincident(g5,g1)
    c: PointOnObject(g5,g-2)
    c: Coincident(g6,g-1)
    c: PointOnObject(g6,g-1)
    c: PointOnObject(g6,g-2)
    c: Equal(g6,g3)
    c: Equal(g3,g4)
    c: Equal(g4,g5)
    c: Coincident(g7,g6)
    c: Coincident(g7,g5)
    c: Vertical(g7)
    c: Coincident(g8,g5)
    c: Coincident(g8,g4)
    c: Horizontal(g8)
    c: Coincident(g9,g4)
    c: Coincident(g9,g3)
    c: Vertical(g9)
    c: Coincident(g10,g3)
    c: Coincident(g10,g6)
    c: Horizontal(g10)
    c: Radius(g6) = 4
FEATURE [PartDesign::Pad] Pad003
  Direction = (1,1,1)
  Length = 2
  Length2 = 100
  Placement = pos=(0,0,7) rot=(0,0,1;0rad)
  Profile = -> Sketch016
  Type = 0
FEATURE [PartDesign::AdditiveLoft] AdditiveLoft
  BaseFeature = -> Pad003
  Closed = false
  Placement = pos=(0,0,7) rot=(0,0,1;0rad)
  Profile = -> Sketch014
  Ruled = false
  Sections = -> [Sketch015]
FEATURE [PartDesign::Pad] Pad004
  BaseFeature = -> AdditiveLoft
  Direction = (1,1,1)
  Length = 2
  Length2 = 100
  Placement = pos=(0,0,7) rot=(0,0,1;0rad)
  Profile = -> Sketch013
  Type = 0
FEATURE [PartDesign::Body] Body001  label="Cover001"
  Group = -> [Sketch013,Sketch014,Sketch015,Sketch016,Pad003,AdditiveLoft,Pad004]
  Origin = -> Origin026
  Tip = -> Pad004
FEATURE [App::Part] Part001  label="Cover"
  Group = -> [Body001]
  Origin = -> Origin025
FEATURE [Part::FeaturePython] ScrewTap026  label="M2.5x20.0-ScrewTap042"  # Fasteners workbench fastener (typed FeaturePython)
  Placement = pos=(0.5,-44,5.355) rot=(1,0,0;1.5708rad)
  diameter = 3
  invert = false
  length = 20
  matchOuter = true
  offset = 0
  thread = true
FEATURE [Part::FeaturePython] ScrewTap027  label="M2.5x20.0-ScrewTap043"  # Fasteners workbench fastener (typed FeaturePython)
  Placement = pos=(10.5,-44,-1.652) rot=(1,0,0;1.5708rad)
  diameter = 3
  invert = false
  length = 20
  matchOuter = true
  offset = 0
  thread = true
FEATURE [Part::FeaturePython] ScrewTap028  label="M2.5x20.0-ScrewTap044"  # Fasteners workbench fastener (typed FeaturePython)
  Placement = pos=(11.498,-44,5.355) rot=(1,0,0;1.5708rad)
  diameter = 3
  invert = false
  length = 20
  matchOuter = true
  offset = 0
  thread = true
FEATURE [Part::FeaturePython] ScrewTap029  label="M2.5x20.0-ScrewTap045"  # Fasteners workbench fastener (typed FeaturePython)
  Placement = pos=(21.505,-44,-1.652) rot=(1,0,0;1.5708rad)
  diameter = 3
  invert = false
  length = 20
  matchOuter = true
  offset = 0
  thread = true
FEATURE [Sketcher::SketchObject] Sketch018
  FullyConstrained = true
  MapMode = 5
  Support = -> [XY_Plane027]
  sketch-geometry (32):
    g0: LineSegment StartX=23 StartY=8.05 StartZ=0 EndX=-1 EndY=8.05 EndZ=0
    g1: LineSegment StartX=-5.85 StartY=1 StartZ=0 EndX=-5.85 EndY=-23 EndZ=0
    g2: LineSegment StartX=-5 StartY=-27.85 StartZ=0 EndX=27 EndY=-27.85 EndZ=0
    g3: LineSegment StartX=27.85 StartY=-23 StartZ=0 EndX=27.85 EndY=1 EndZ=0
    g4: ArcOfCircle CenterX=23 CenterY=10.05 CenterZ=0 NormalX=0 NormalY=0 NormalZ=1 AngleXU=0 Radius=2 StartAngle=4.71239 EndAngle=6.28319
    g5: ArcOfCircle CenterX=29.85 CenterY=1 CenterZ=0 NormalX=0 NormalY=0 NormalZ=1 AngleXU=0 Radius=2 StartAngle=1.5708 EndAngle=3.14159
    g6: ArcOfCircle CenterX=-7.85 CenterY=-23 CenterZ=0 NormalX=0 NormalY=0 NormalZ=1 AngleXU=0 Radius=2 StartAngle=4.71239 EndAngle=6.28319
    g7: ArcOfCircle CenterX=-5 CenterY=-29.85 CenterZ=0 NormalX=0 NormalY=0 NormalZ=1 AngleXU=0 Radius=2 StartAngle=1.5708 EndAngle=3.14159
    g8: ArcOfCircle CenterX=27 CenterY=-29.85 CenterZ=0 NormalX=0 NormalY=0 NormalZ=1 AngleXU=0 Radius=2 StartAngle=0 EndAngle=1.5708
    g9: ArcOfCircle CenterX=29.85 CenterY=-23 CenterZ=0 NormalX=0 NormalY=0 NormalZ=1 AngleXU=0 Radius=2 StartAngle=3.14159 EndAngle=4.71239
    g10: ArcOfCircle CenterX=-1 CenterY=10.05 CenterZ=0 NormalX=0 NormalY=0 NormalZ=1 AngleXU=0 Radius=2 StartAngle=3.14159 EndAngle=4.71239
    g11: ArcOfCircle CenterX=-7.85 CenterY=1 CenterZ=0 NormalX=0 NormalY=0 NormalZ=1 AngleXU=0 Radius=2 StartAngle=0 EndAngle=1.5708
    g12: LineSegment StartX=25 StartY=10.05 StartZ=0 EndX=25 EndY=16 EndZ=0
    g13: LineSegment StartX=25 StartY=16 StartZ=0 EndX=38 EndY=16 EndZ=0
    g14: LineSegment StartX=38 StartY=16 StartZ=0 EndX=38 EndY=3 EndZ=0
    g15: LineSegment StartX=29.85 StartY=3 StartZ=0 EndX=38 EndY=3 EndZ=0
    g16: LineSegment StartX=-7.85 StartY=-25 StartZ=0 EndX=-16 EndY=-25 EndZ=0
    g17: LineSegment StartX=-16 StartY=-25 StartZ=0 EndX=-16 EndY=-38 EndZ=0
    g18: LineSegment StartX=-16 StartY=-38 StartZ=0 EndX=-7 EndY=-38 EndZ=0
    g19: LineSegment StartX=-7 StartY=-29.85 StartZ=0 EndX=-7 EndY=-38 EndZ=0
    g20: LineSegment StartX=29.85 StartY=-25 StartZ=0 EndX=38 EndY=-25 EndZ=0
    g21: LineSegment StartX=38 StartY=-25 StartZ=0 EndX=38 EndY=-38 EndZ=0
    g22: LineSegment StartX=38 StartY=-38 StartZ=0 EndX=29 EndY=-38 EndZ=0
    g23: LineSegment StartX=29 StartY=-38 StartZ=0 EndX=29 EndY=-29.85 EndZ=0
    g24: LineSegment StartX=-3 StartY=10.05 StartZ=0 EndX=-3 EndY=16 EndZ=0
    g25: LineSegment StartX=-3 StartY=16 StartZ=0 EndX=-16 EndY=16 EndZ=0
    g26: LineSegment StartX=-16 StartY=16 StartZ=0 EndX=-16 EndY=3 EndZ=0
    g27: LineSegment StartX=-7.85 StartY=3 StartZ=0 EndX=-16 EndY=3 EndZ=0
    g28: GeomPoint X=31.5 Y=9.5 Z=0
    g29: GeomPoint X=-9.5 Y=9.5 Z=0
    g30: GeomPoint X=-9.5 Y=-31.5 Z=0
    g31: GeomPoint X=31.5 Y=-31.5 Z=0
  constraints (98):
    c: Horizontal(g0)
    c: Horizontal(g2)
    c: Vertical(g1)
    c: Vertical(g3)
    c: Equal(g6,g7)
    c: Equal(g7,g8)
    c: Equal(g8,g9)
    c: Equal(g9,g5)
    c: Equal(g5,g4)
    c: Equal(g4,g10)
    c: Equal(g10,g11)
    c: Vertical(g8,g8)
    c: Vertical(g4,g4)
    c: Horizontal(g9,g9)
    c: Horizontal(g9,g6)
    c: Horizontal(g6,g6)
    c: Horizontal(g11,g11)
    c: Horizontal(g11,g5)
    c: Horizontal(g5,g5)
    c: Vertical(g10,g10)
    c: Vertical(g7,g7)
    c: Coincident(g0,g10)
    c: Coincident(g2,g7)
    c: Coincident(g6,g1)
    c: Horizontal(g7,g7)
    c: Horizontal(g8,g8)
    c: Coincident(g9,g3)
    c: Vertical(g6,g6)
    c: Vertical(g11,g11)
    c: Vertical(g9,g9)
    c: Vertical(g5,g5)
    c: Coincident(g0,g4)
    c: Horizontal(g10,g10)
    c: Horizontal(g4,g4)
    c: Coincident(g5,g3)
    c: Coincident(g1,g11)
    c: Coincident(g12,g4)
    c: Vertical(g12)
    c: Coincident(g13,g12)
    c: Horizontal(g13)
    c: Coincident(g14,g13)
    c: Vertical(g14)
    c: Coincident(g15,g5)
    c: Coincident(g15,g14)
    c: Horizontal(g15)
    c: Equal(g13,g14)
    c: DistanceX(g13,g13) = 13
    c: Coincident(g16,g6)
    c: Horizontal(g16)
    c: Coincident(g17,g16)
    c: Vertical(g17)
    c: Coincident(g18,g17)
    c: Horizontal(g18)
    c: Coincident(g19,g7)
    c: Coincident(g19,g18)
    c: Vertical(g19)
    c: Equal(g16,g19)
    c: Equal(g19,g15)
    c: Coincident(g20,g9)
    c: Horizontal(g20)
    c: Coincident(g21,g20)
    c: Vertical(g21)
    c: Coincident(g22,g21)
    c: Horizontal(g22)
    c: Coincident(g23,g22)
    c: Coincident(g23,g8)
    c: Vertical(g23)
    c: Equal(g14,g21)
    c: Coincident(g24,g10)
    c: Vertical(g24)
    c: Coincident(g25,g24)
    c: Horizontal(g25)
    c: Coincident(g26,g25)
    c: Vertical(g26)
    c: Coincident(g27,g11)
    c: Coincident(g27,g26)
    c: Horizontal(g27)
    c: DistanceX(g0,g0) = 24
    c: DistanceX(g1,g-1) = 5.85
    c: Radius(g10) = 2
    c: DistanceY(g1,g1) = 24
    c: Coincident(g2,g8)
    c: DistanceX(g-1,g0) = -1
    c: DistanceY(g2,g-1) = 27.85
    c: DistanceY(g-1,g0) = 8.05
    c: Horizontal(g13,g25)
    c: Vertical(g25,g17)
    c: Horizontal(g31,g30)
    c: Vertical(g29,g30)
    c: Vertical(g28,g31)
    c: Symmetric(g14,g12,g28)
    c: Symmetric(g24,g26,g29)
    c: DistanceY(g30,g6) = 6.5
    c: Equal(g17,g14)
    c: Equal(g22,g18)
    c: Equal(g20,g15)
    c: DistanceX(g1,g3) = 33.7
    c: DistanceX(g2,g2) = 32
FEATURE [Sketcher::SketchObject] Sketch017
  AttachmentOffset = pos=(0,0,7) rot=(0,0,1;0rad)
  ExternalGeometry = -> [Sketch018]
  FullyConstrained = true
  MapMode = 2
  sketch-geometry (36):
    g0: ArcOfCircle CenterX=22 CenterY=-1.4e-15 CenterZ=0 NormalX=0 NormalY=0 NormalZ=1 AngleXU=0 Radius=4.2 StartAngle=0 EndAngle=1.5708
    g1: ArcOfCircle CenterX=-1.47e-14 CenterY=0 CenterZ=0 NormalX=0 NormalY=0 NormalZ=1 AngleXU=0 Radius=4.2 StartAngle=1.5708 EndAngle=3.14159
    g2: ArcOfCircle CenterX=-1.47e-14 CenterY=-22 CenterZ=0 NormalX=0 NormalY=0 NormalZ=1 AngleXU=0 Radius=4.2 StartAngle=3.14159 EndAngle=4.71239
    g3: ArcOfCircle CenterX=22 CenterY=-22 CenterZ=0 NormalX=0 NormalY=0 NormalZ=1 AngleXU=0 Radius=4.2 StartAngle=4.71239 EndAngle=6.28319
    g4: LineSegment StartX=-1.47e-14 StartY=4.2 StartZ=0 EndX=22 EndY=4.2 EndZ=0
    g5: LineSegment StartX=26.2 StartY=-1.4e-15 StartZ=0 EndX=26.2 EndY=-22 EndZ=0
    g6: LineSegment StartX=-4.2 StartY=-1.4e-15 StartZ=0 EndX=-4.2 EndY=-22 EndZ=0
    g7: LineSegment StartX=-1.47e-14 StartY=-26.2 StartZ=0 EndX=22 EndY=-26.2 EndZ=0
    g8: LineSegment StartX=27.85 StartY=1 StartZ=0 EndX=27.85 EndY=-23 EndZ=0
    g9: LineSegment StartX=27 StartY=-27.85 StartZ=0 EndX=-5 EndY=-27.85 EndZ=0
    g10: LineSegment StartX=-7 StartY=-38 StartZ=0 EndX=-16 EndY=-38 EndZ=0
    g11: LineSegment StartX=-16 StartY=-38 StartZ=0 EndX=-16 EndY=-25 EndZ=0
    g12: LineSegment StartX=-5.85 StartY=-23 StartZ=0 EndX=-5.85 EndY=1 EndZ=0
    g13: LineSegment StartX=-1 StartY=8.05 StartZ=0 EndX=23 EndY=8.05 EndZ=0
    g14: ArcOfCircle CenterX=29.85 CenterY=1 CenterZ=0 NormalX=0 NormalY=0 NormalZ=1 AngleXU=0 Radius=2 StartAngle=1.5708 EndAngle=3.14159
    g15: ArcOfCircle CenterX=23 CenterY=10.05 CenterZ=0 NormalX=0 NormalY=0 NormalZ=1 AngleXU=0 Radius=2 StartAngle=4.71239 EndAngle=6.28319
    g16: ArcOfCircle CenterX=-1 CenterY=10.05 CenterZ=0 NormalX=0 NormalY=0 NormalZ=1 AngleXU=0 Radius=2 StartAngle=3.14159 EndAngle=4.71239
    g17: ArcOfCircle CenterX=-7.85 CenterY=1 CenterZ=0 NormalX=0 NormalY=0 NormalZ=1 AngleXU=0 Radius=2 StartAngle=0 EndAngle=1.5708
    g18: ArcOfCircle CenterX=-7.85 CenterY=-23 CenterZ=0 NormalX=0 NormalY=0 NormalZ=1 AngleXU=0 Radius=2 StartAngle=4.71239 EndAngle=6.28319
    g19: ArcOfCircle CenterX=29.85 CenterY=-23 CenterZ=0 NormalX=0 NormalY=0 NormalZ=1 AngleXU=0 Radius=2 StartAngle=3.14159 EndAngle=4.71239
    g20: ArcOfCircle CenterX=27 CenterY=-29.85 CenterZ=0 NormalX=0 NormalY=0 NormalZ=1 AngleXU=0 Radius=2 StartAngle=0 EndAngle=1.5708
    g21: ArcOfCircle CenterX=-5 CenterY=-29.85 CenterZ=0 NormalX=0 NormalY=0 NormalZ=1 AngleXU=0 Radius=2 StartAngle=1.5708 EndAngle=3.14159
    g22: LineSegment StartX=25 StartY=16 StartZ=0 EndX=38 EndY=16 EndZ=0
    g23: LineSegment StartX=38 StartY=16 StartZ=0 EndX=38 EndY=3 EndZ=0
    g24: LineSegment StartX=38 StartY=3 StartZ=0 EndX=29.85 EndY=3 EndZ=0
    g25: LineSegment StartX=25 StartY=10.05 StartZ=0 EndX=25 EndY=16 EndZ=0
    g26: LineSegment StartX=-3 StartY=10.05 StartZ=0 EndX=-3 EndY=16 EndZ=0
    g27: LineSegment StartX=-3 StartY=16 StartZ=0 EndX=-16 EndY=16 EndZ=0
    g28: LineSegment StartX=-16 StartY=16 StartZ=0 EndX=-16 EndY=3 EndZ=0
    g29: LineSegment StartX=-16 StartY=3 StartZ=0 EndX=-7.85 EndY=3 EndZ=0
    g30: LineSegment StartX=-16 StartY=-25 StartZ=0 EndX=-7.85 EndY=-25 EndZ=0
    g31: LineSegment StartX=-7 StartY=-38 StartZ=0 EndX=-7 EndY=-29.85 EndZ=0
    g32: LineSegment StartX=29 StartY=-29.85 StartZ=0 EndX=29 EndY=-38 EndZ=0
    g33: LineSegment StartX=29 StartY=-38 StartZ=0 EndX=38 EndY=-38 EndZ=0
    g34: LineSegment StartX=38 StartY=-38 StartZ=0 EndX=38 EndY=-25 EndZ=0
    g35: LineSegment StartX=38 StartY=-25 StartZ=0 EndX=29.85 EndY=-25 EndZ=0
  constraints (91):
    c: Coincident(g5,g0)
    c: Coincident(g5,g3)
    c: Vertical(g5)
    c: Coincident(g6,g1)
    c: Coincident(g6,g2)
    c: Vertical(g6)
    c: Coincident(g7,g2)
    c: Coincident(g7,g3)
    c: Horizontal(g7)
    c: Radius(g1) = 4.2
    c: Horizontal(g0,g0)
    c: Horizontal(g0,g1)
    c: Vertical(g0,g0)
    c: Vertical(g0,g3)
    c: Vertical(g3,g3)
    c: Vertical(g2,g2)
    c: Vertical(g2,g1)
    c: Coincident(g4,g1)
    c: Horizontal(g4)
    c: Coincident(g0,g4)
    c: DistanceX(g1,g0) = 22
    c: DistanceY(g3,g0) = 22
    c: Horizontal(g2,g2)
    c: Equal(g3,g2)
    c: Equal(g2,g0)
    c: Coincident(g1,g-1)
    c: Coincident(g11,g10)
    c: Coincident(g14,g8)
    c: Coincident(g15,g13)
    c: Coincident(g16,g13)
    c: Coincident(g17,g12)
    c: Coincident(g18,g12)
    c: Coincident(g19,g8)
    c: Coincident(g20,g9)
    c: Coincident(g21,g9)
    c: Coincident(g23,g22)
    c: Coincident(g24,g23)
    c: Coincident(g24,g14)
    c: Coincident(g25,g15)
    c: Coincident(g25,g22)
    c: Coincident(g26,g16)
    c: Coincident(g27,g26)
    c: Coincident(g28,g27)
    c: Coincident(g29,g28)
    c: Coincident(g29,g17)
    c: Coincident(g30,g11)
    c: Coincident(g30,g18)
    c: Coincident(g31,g10)
    c: Coincident(g31,g21)
    c: Coincident(g32,g20)
    c: Coincident(g33,g32)
    c: Coincident(g34,g33)
    c: Coincident(g35,g34)
    c: Coincident(g35,g19)
    c: Vertical(g1,g1)
    c: Coincident(g12,g-5)
    c: Coincident(g17,g-5)
    c: Vertical(g17,g17)
    c: Coincident(g28,g-17)
    c: Coincident(g13,g-4)
    c: Coincident(g16,g-4)
    c: Coincident(g26,g-16)
    c: Coincident(g13,g-3)
    c: Coincident(g-3,g15)
    c: Coincident(g22,g-15)
    c: Coincident(g19,g-7)
    c: Coincident(g8,g-7)
    c: Coincident(g34,g-12)
    c: Coincident(g8,g-18)
    c: Coincident(g14,g-18)
    c: Coincident(g23,g-14)
    c: Coincident(g12,g-6)
    c: Coincident(g18,g-6)
    c: Coincident(g11,g-13)
    c: Coincident(g-17,g27)
    c: Coincident(g22,g-15)
    c: Horizontal(g15,g15)
    c: Horizontal(g16,g16)
    c: Coincident(g-13,g10)
    c: Coincident(g33,g-12)
    c: Coincident(g9,g-8)
    c: Coincident(g20,g-8)
    c: Horizontal(g20,g20)
    c: Coincident(g9,g-9)
    c: Horizontal(g21,g21)
    c: Coincident(g-9,g21)
    c: Coincident(g-10,g10)
    c: Vertical(g18,g18)
    c: Coincident(g-11,g32)
    c: Vertical(g19,g19)
    c: Vertical(g14,g14)
FEATURE [PartDesign::Pad] Pad005
  Direction = (1,1,1)
  Length = 5
  Length2 = 100
  Profile = -> Sketch018
  Reversed = true
  Type = 0
FEATURE [PartDesign::Pad] Pad006
  BaseFeature = -> Pad005
  Direction = (1,1,1)
  Length = 9
  Length2 = 100
  Profile = -> Sketch017
  Type = 0
FEATURE [Sketcher::SketchObject] Sketch019
  AttachmentOffset = pos=(0,0,8.5) rot=(0,0,1;0rad)
  ExternalGeometry = -> [Sketch018,Sketch017]
  FullyConstrained = true
  MapMode = 5
  Placement = pos=(0,0,8.5) rot=(0,0,1;0rad)
  Support = -> [XY_Plane027]
  sketch-geometry (12):
    g0: LineSegment StartX=38 StartY=16 StartZ=0 EndX=-16 EndY=16 EndZ=0
    g1: LineSegment StartX=-16 StartY=16 StartZ=0 EndX=-16 EndY=-38 EndZ=0
    g2: LineSegment StartX=-16 StartY=-38 StartZ=0 EndX=38 EndY=-38 EndZ=0
    g3: LineSegment StartX=38 StartY=-38 StartZ=0 EndX=38 EndY=16 EndZ=0
    g4: ArcOfCircle CenterX=22 CenterY=-22 CenterZ=0 NormalX=0 NormalY=0 NormalZ=1 AngleXU=0 Radius=4.2 StartAngle=4.71239 EndAngle=6.28319
    g5: ArcOfCircle CenterX=22 CenterY=-6e-16 CenterZ=0 NormalX=0 NormalY=0 NormalZ=1 AngleXU=0 Radius=4.2 StartAngle=0 EndAngle=1.5708
    g6: ArcOfCircle CenterX=0 CenterY=0 CenterZ=0 NormalX=0 NormalY=0 NormalZ=1 AngleXU=0 Radius=4.2 StartAngle=1.5708 EndAngle=3.14159
    g7: ArcOfCircle CenterX=-8e-16 CenterY=-22 CenterZ=0 NormalX=0 NormalY=0 NormalZ=1 AngleXU=0 Radius=4.2 StartAngle=3.14159 EndAngle=4.71239
    g8: LineSegment StartX=22 StartY=4.2 StartZ=0 EndX=0 EndY=4.2 EndZ=0
    g9: LineSegment StartX=-4.2 StartY=-1.4e-15 StartZ=0 EndX=-4.2 EndY=-22 EndZ=0
    g10: LineSegment StartX=-1.6e-15 StartY=-26.2 StartZ=0 EndX=22 EndY=-26.2 EndZ=0
    g11: LineSegment StartX=26.2 StartY=-22 StartZ=0 EndX=26.2 EndY=0 EndZ=0
  constraints (30):
    c: Coincident(g0,g1)
    c: Coincident(g1,g2)
    c: Coincident(g2,g3)
    c: Coincident(g3,g0)
    c: Horizontal(g0)
    c: Horizontal(g2)
    c: Vertical(g1)
    c: Vertical(g3)
    c: Coincident(g0,g-3)
    c: Coincident(g1,g-5)
    c: Coincident(g4,g-10)
    c: Coincident(g4,g-10)
    c: Coincident(g4,g-10)
    c: Coincident(g5,g-7)
    c: Coincident(g5,g-7)
    c: Coincident(g5,g-7)
    c: Coincident(g6,g-1)
    c: Coincident(g6,g-9)
    c: Coincident(g6,g-9)
    c: Coincident(g7,g-8)
    c: Coincident(g7,g-8)
    c: Coincident(g7,g-8)
    c: Coincident(g8,g5)
    c: Coincident(g8,g6)
    c: Coincident(g9,g6)
    c: Coincident(g9,g7)
    c: Coincident(g10,g7)
    c: Coincident(g10,g4)
    c: Coincident(g11,g4)
    c: Coincident(g11,g5)
FEATURE [PartDesign::Pad] Pad007
  BaseFeature = -> Pad006
  Direction = (1,1,1)
  Length = 3.5
  Length2 = 100
  Profile = -> Sketch019
  Type = 0
FEATURE [Sketcher::SketchObject] Sketch020
  AttachmentOffset = pos=(0,0,12) rot=(0,0,1;0rad)
  ExternalGeometry = -> [Sketch019]
  FullyConstrained = true
  MapMode = 5
  Placement = pos=(0,0,12) rot=(0,0,1;0rad)
  Support = -> [XY_Plane027]
  sketch-geometry (16):
    g0: ArcOfCircle CenterX=22 CenterY=-6e-16 CenterZ=0 NormalX=0 NormalY=0 NormalZ=1 AngleXU=0 Radius=5.5 StartAngle=1e-16 EndAngle=1.5708
    g1: ArcOfCircle CenterX=22 CenterY=-6e-16 CenterZ=0 NormalX=0 NormalY=0 NormalZ=1 AngleXU=0 Radius=8.5 StartAngle=1e-16 EndAngle=1.5708
    g2: ArcOfCircle CenterX=0 CenterY=0 CenterZ=0 NormalX=0 NormalY=0 NormalZ=1 AngleXU=0 Radius=5.5 StartAngle=1.5708 EndAngle=3.14159
    g3: ArcOfCircle CenterX=0 CenterY=0 CenterZ=0 NormalX=0 NormalY=0 NormalZ=1 AngleXU=0 Radius=8.5 StartAngle=1.5708 EndAngle=3.14159
    g4: LineSegment StartX=5e-16 StartY=8.5 StartZ=0 EndX=22 EndY=8.5 EndZ=0
    g5: LineSegment StartX=3e-16 StartY=5.5 StartZ=0 EndX=22 EndY=5.5 EndZ=0
    g6: ArcOfCircle CenterX=22 CenterY=-22 CenterZ=0 NormalX=0 NormalY=0 NormalZ=1 AngleXU=0 Radius=5.5 StartAngle=4.71239 EndAngle=6.28319
    g7: ArcOfCircle CenterX=22 CenterY=-22 CenterZ=0 NormalX=0 NormalY=0 NormalZ=1 AngleXU=0 Radius=8.5 StartAngle=4.71239 EndAngle=6.28319
    g8: ArcOfCircle CenterX=-5.8e-15 CenterY=-22 CenterZ=0 NormalX=0 NormalY=0 NormalZ=1 AngleXU=0 Radius=5.5 StartAngle=3.14159 EndAngle=4.71239
    g9: ArcOfCircle CenterX=-5.8e-15 CenterY=-22 CenterZ=0 NormalX=0 NormalY=0 NormalZ=1 AngleXU=0 Radius=8.5 StartAngle=3.14159 EndAngle=4.71239
    g10: LineSegment StartX=-5.5 StartY=-22 StartZ=0 EndX=-5.5 EndY=0 EndZ=0
    g11: LineSegment StartX=-8.5 StartY=1e-15 StartZ=0 EndX=-8.5 EndY=-22 EndZ=0
    g12: LineSegment StartX=-5.8e-15 StartY=-27.5 StartZ=0 EndX=22 EndY=-27.5 EndZ=0
    g13: LineSegment StartX=-6.4e-15 StartY=-30.5 StartZ=0 EndX=22 EndY=-30.5 EndZ=0
    g14: LineSegment StartX=27.5 StartY=-22 StartZ=0 EndX=27.5 EndY=0 EndZ=0
    g15: LineSegment StartX=30.5 StartY=3e-16 StartZ=0 EndX=30.5 EndY=-22 EndZ=0
  constraints (49):
    c: Coincident(g0,g-7)
    c: PointOnObject(g0,g-1)
    c: Coincident(g1,g0)
    c: PointOnObject(g1,g-1)
    c: PointOnObject(g2,g-2)
    c: PointOnObject(g2,g-1)
    c: PointOnObject(g3,g-2)
    c: PointOnObject(g3,g-1)
    c: Coincident(g4,g3)
    c: Coincident(g4,g1)
    c: Horizontal(g4)
    c: Tangent(g4,g1)
    c: Coincident(g5,g2)
    c: Coincident(g5,g0)
    c: Horizontal(g5)
    c: Coincident(g6,g-8)
    c: Coincident(g7,g6)
    c: PointOnObject(g9,g-2)
    c: Coincident(g10,g8)
    c: Coincident(g10,g2)
    c: Vertical(g10)
    c: Coincident(g11,g3)
    c: Coincident(g11,g9)
    c: Vertical(g11)
    c: Coincident(g12,g8)
    c: Coincident(g12,g6)
    c: Horizontal(g12)
    c: Coincident(g13,g9)
    c: Coincident(g13,g7)
    c: Horizontal(g13)
    c: Coincident(g14,g6)
    c: Coincident(g14,g0)
    c: Vertical(g14)
    c: Coincident(g15,g1)
    c: Coincident(g15,g7)
    c: Coincident(g3,g-1)
    c: Coincident(g2,g3)
    c: Vertical(g0,g1)
    c: Vertical(g6,g7)
    c: Vertical(g7,g6)
    c: Horizontal(g8,g9)
    c: Radius(g8) = 5.5
    c: Radius(g9) = 8.5
    c: Horizontal(g7,g6)
    c: Coincident(g8,g9)
    c: Coincident(g8,g-5)
    c: Vertical(g8,g8)
    c: Horizontal(g8,g8)
    c: DistanceX(g4,g4) = 22
FEATURE [PartDesign::Pocket] Pocket005
  BaseFeature = -> Pad007
  Length = 2.8
  Length2 = 100
  Profile = -> Sketch020
  Type = 0
FEATURE [Part::FeaturePython] ScrewTap030  label="M3x20.0-ScrewTap008"  # Fasteners workbench fastener (typed FeaturePython)
  Placement = pos=(0,0,10) rot=(0,0,1;0rad)
  diameter = 4
  invert = false
  length = 20
  matchOuter = true
  offset = 0
  thread = true
FEATURE [Part::FeaturePython] ScrewTap031  label="M3x20.0-ScrewTap009"  # Fasteners workbench fastener (typed FeaturePython)
  Placement = pos=(22,0,10) rot=(0,0,1;0rad)
  diameter = 4
  invert = false
  length = 20
  matchOuter = true
  offset = 0
  thread = true
FEATURE [Part::FeaturePython] ScrewTap032  label="M3x20.0-ScrewTap010"  # Fasteners workbench fastener (typed FeaturePython)
  Placement = pos=(22,-22,10) rot=(0,0,1;0rad)
  diameter = 4
  invert = false
  length = 20
  matchOuter = true
  offset = 0
  thread = true
FEATURE [Part::FeaturePython] ScrewTap033  label="M3x20.0-ScrewTap011"  # Fasteners workbench fastener (typed FeaturePython)
  Placement = pos=(0,-22,10) rot=(0,0,1;0rad)
  diameter = 4
  invert = false
  length = 20
  matchOuter = true
  offset = 0
  thread = true
FEATURE [Part::FeaturePython] ScrewTap034  label="M3x20.0-ScrewTap023"  # Fasteners workbench fastener (typed FeaturePython)
  Placement = pos=(-12,-34,12) rot=(0,0,1;0rad)
  diameter = 4
  invert = false
  length = 20
  matchOuter = true
  offset = 0
  thread = true
FEATURE [Part::FeaturePython] ScrewTap035  label="M3x20.0-ScrewTap026"  # Fasteners workbench fastener (typed FeaturePython)
  Placement = pos=(-12,12,12) rot=(0,0,1;0rad)
  diameter = 4
  invert = false
  length = 20
  matchOuter = true
  offset = 0
  thread = true
FEATURE [Part::FeaturePython] ScrewTap036  label="M3x20.0-ScrewTap024"  # Fasteners workbench fastener (typed FeaturePython)
  Placement = pos=(34,-34,12) rot=(0,0,1;0rad)
  diameter = 4
  invert = false
  length = 20
  matchOuter = true
  offset = 0
  thread = true
FEATURE [Part::FeaturePython] ScrewTap037  label="M3x20.0-ScrewTap025"  # Fasteners workbench fastener (typed FeaturePython)
  Placement = pos=(34,12,12) rot=(0,0,1;0rad)
  diameter = 4
  invert = false
  length = 20
  matchOuter = true
  offset = 0
  thread = true
FEATURE [Part::FeaturePython] ScrewTap038  label="M2.5x20.0-ScrewTap017"  # Fasteners workbench fastener (typed FeaturePython)
  Placement = pos=(4.9,-5,2.25) rot=(1,0,0;1.5708rad)
  diameter = 3
  invert = false
  length = 20
  matchOuter = true
  offset = 0
  thread = true
FEATURE [Part::FeaturePython] ScrewTap039  label="M2.5x50.0-ScrewTap004"  # Fasteners workbench fastener (typed FeaturePython)
  Placement = pos=(36.1,-17.1,1.85) rot=(0,1,0;1.5708rad)
  diameter = 3
  invert = false
  length = 50
  matchOuter = true
  offset = 0
  thread = true
FEATURE [Part::FeaturePython] ScrewTap040  label="M2.5x20.0-ScrewTap018"  # Fasteners workbench fastener (typed FeaturePython)
  Placement = pos=(17.1,-5,2.25) rot=(1,0,0;1.5708rad)
  diameter = 3
  invert = false
  length = 20
  matchOuter = true
  offset = 0
  thread = true
FEATURE [Part::FeaturePython] ScrewTap041  label="M2.5x50.0-ScrewTap003"  # Fasteners workbench fastener (typed FeaturePython)
  Placement = pos=(36.1,-4.895,1.85) rot=(0,1,0;1.5708rad)
  diameter = 3
  invert = false
  length = 50
  matchOuter = true
  offset = 0
  thread = true
FEATURE [PartDesign::Boolean] Boolean005
  BaseFeature = -> Pocket005
  Group = -> [ScrewTap030]
  Refine = true
  Type = 1
FEATURE [PartDesign::Boolean] Boolean006
  BaseFeature = -> Boolean005
  Group = -> [ScrewTap031]
  Refine = true
  Type = 1
FEATURE [PartDesign::Boolean] Boolean007
  BaseFeature = -> Boolean006
  Group = -> [ScrewTap032]
  Refine = true
  Type = 1
FEATURE [PartDesign::Boolean] Boolean008
  BaseFeature = -> Boolean007
  Group = -> [ScrewTap033,ScrewTap034,ScrewTap035,ScrewTap036,ScrewTap037]
  Refine = true
  Type = 1
FEATURE [PartDesign::Boolean] Boolean009
  BaseFeature = -> Boolean008
  Group = -> [ScrewTap038,ScrewTap039,ScrewTap040,ScrewTap041]
  Refine = true
  Type = 1
FEATURE [Sketcher::SketchObject] Sketch021
  AttachmentOffset = pos=(0,0,28) rot=(0,0,1;0rad)
  FullyConstrained = true
  MapMode = 5
  Placement = pos=(28,-6.2e-15,6.2e-15) rot=(0.57735,0.57735,0.57735;2.0944rad)
  Support = -> [YZ_Plane027]
  sketch-geometry (1):
    g0: Circle CenterX=-11 CenterY=1.85 CenterZ=0 NormalX=0 NormalY=0 NormalZ=1 AngleXU=0 Radius=1.9
  constraints (3):
    c: DistanceY(g-1,g0) = 1.85
    c: Radius(g0) = 1.9
    c: DistanceX(g0,g-1) = 11
FEATURE [PartDesign::Pocket] Pocket006
  BaseFeature = -> Boolean009
  Length = 2
  Length2 = 100
  Profile = -> Sketch021
  Type = 0
FEATURE [Sketcher::SketchObject] Sketch022
  AttachmentOffset = pos=(0,0,-9) rot=(0,0,1;0rad)
  FullyConstrained = true
  MapMode = 5
  Placement = pos=(0,9,2e-15) rot=(1,0,0;1.5708rad)
  Support = -> [XZ_Plane027]
  sketch-geometry (1):
    g0: Circle CenterX=11 CenterY=2.25 CenterZ=0 NormalX=0 NormalY=0 NormalZ=1 AngleXU=0 Radius=1.9
  constraints (3):
    c: DistanceX(g-1,g0) = 11
    c: DistanceY(g-1,g0) = 2.25
    c: Radius(g0) = 1.9
FEATURE [Sketcher::SketchObject] Sketch023
  AttachmentOffset = pos=(0,0,28) rot=(0,0,1;0rad)
  FullyConstrained = true
  MapMode = 5
  Placement = pos=(0,-28,-6.2e-15) rot=(1,0,0;1.5708rad)
  Support = -> [XZ_Plane027]
  sketch-geometry (2):
    g0: Circle CenterX=5.5 CenterY=1.85 CenterZ=0 NormalX=0 NormalY=0 NormalZ=1 AngleXU=0 Radius=1.9
    g1: Circle CenterX=16.5 CenterY=1.85 CenterZ=0 NormalX=0 NormalY=0 NormalZ=1 AngleXU=0 Radius=1.9
  constraints (6):
    c: DistanceX(g-1,g0) = 5.5
    c: DistanceY(g-1,g0) = 1.85
    c: Radius(g0) = 1.9
    c: Horizontal(g1,g0)
    c: Equal(g0,g1)
    c: DistanceX(g0,g1) = 11
FEATURE [PartDesign::Pocket] Pocket009
  BaseFeature = -> Pocket006
  Length = 2
  Length2 = 100
  Profile = -> Sketch023
  Type = 0
FEATURE [PartDesign::Pocket] Pocket007
  BaseFeature = -> Pocket009
  Length = 5
  Length2 = 100
  Profile = -> Sketch022
  Reversed = true
  Type = 0
FEATURE [Sketcher::SketchObject] Sketch024
  AttachmentOffset = pos=(0,0,-6) rot=(0,0,1;0rad)
  ExternalGeometry = -> [Sketch021]
  FullyConstrained = true
  MapMode = 5
  Placement = pos=(-6,1.3e-15,-1.3e-15) rot=(0.57735,0.57735,0.57735;2.0944rad)
  Support = -> [YZ_Plane027]
  sketch-geometry (1):
    g0: Circle CenterX=-11 CenterY=1.85 CenterZ=0 NormalX=0 NormalY=0 NormalZ=1 AngleXU=0 Radius=1.9
  constraints (2):
    c: Coincident(g0,g-3)
    c: Tangent(g0,g-3)
FEATURE [PartDesign::Pocket] Pocket008
  BaseFeature = -> Pocket007
  Length = 2
  Length2 = 100
  Profile = -> Sketch024
  Reversed = true
  Type = 0
FEATURE [Part::Feature] Part__Feature023  label="COMPOUND008"
  shape: bbox 10.68 x 16.99 x 9.525 mm, 25 faces (baked)
FEATURE [Part::Feature] Part__Feature024  label="COMPOUND009"
  shape: bbox 3.915 x 4.521 x 7.92 mm, 9 faces (baked)
FEATURE [App::Part] COMPOUND002  label="COMPOUND010"
  Group = -> [Part__Feature023,Part__Feature024]
  Origin = -> Origin029
FEATURE [App::Part] _42_1701_626002  label="142-1701-628"
  Group = -> [COMPOUND002]
  Origin = -> Origin030
  Placement = pos=(5.5,-16.285,1.85) rot=(0.345437,0.663579,-0.663579;2.47638rad)
FEATURE [Part::Feature] Part__Feature025  label="COMPOUND011"
  shape: bbox 10.68 x 16.99 x 9.525 mm, 25 faces (baked)
FEATURE [Part::Feature] Part__Feature026  label="COMPOUND012"
  shape: bbox 3.915 x 4.521 x 7.92 mm, 9 faces (baked)
FEATURE [App::Part] COMPOUND003  label="COMPOUND013"
  Group = -> [Part__Feature025,Part__Feature026]
  Origin = -> Origin031
FEATURE [App::Part] _42_1701_626003  label="142-1701-629"
  Group = -> [COMPOUND003]
  Origin = -> Origin032
  Placement = pos=(16.946,0,1.85) rot=(0,1,0;1.5708rad)
FEATURE [Part::Feature] Part__Feature027  label="COMPOUND014"
  shape: bbox 10.7 x 16.7 x 16.53 mm, 35 faces (baked)
FEATURE [App::Part] _32147_48001  label="132147-049"
  Group = -> [Part__Feature027]
  Origin = -> Origin033
  Placement = pos=(7e-16,19.096,2.25) rot=(-0.57735,0.57735,0.57735;2.0944rad)
FEATURE [Part::Feature] Part__Feature028  label="COMPOUND015"
  shape: bbox 10.68 x 16.99 x 9.525 mm, 25 faces (baked)
FEATURE [Part::Feature] Part__Feature029  label="COMPOUND016"
  shape: bbox 3.915 x 4.521 x 7.92 mm, 9 faces (baked)
FEATURE [App::Part] COMPOUND004  label="COMPOUND017"
  Group = -> [Part__Feature028,Part__Feature029]
  Origin = -> Origin034
FEATURE [App::Part] _42_1701_626004  label="142-1701-630"
  Group = -> [COMPOUND004]
  Origin = -> Origin035
  Placement = pos=(-16.692,6e-16,1.85) rot=(-0.707107,0,0.707107;3.14159rad)
FEATURE [Part::Feature] Part__Feature030  label="COMPOUND018"
  shape: bbox 10.68 x 16.99 x 9.525 mm, 25 faces (baked)
FEATURE [Part::Feature] Part__Feature031  label="COMPOUND019"
  shape: bbox 3.915 x 4.521 x 7.92 mm, 9 faces (baked)
FEATURE [App::Part] COMPOUND005  label="COMPOUND020"
  Group = -> [Part__Feature030,Part__Feature031]
  Origin = -> Origin036
FEATURE [App::Part] _42_1701_626005  label="142-1701-631"
  Group = -> [COMPOUND005]
  Origin = -> Origin037
  Placement = pos=(-5.5,-16.285,1.85) rot=(0.345437,0.663579,-0.663579;2.47638rad)
FEATURE [Part::Feature] Part__Feature032  label="LTC5548 PCB"
  shape: bbox 30 x 30 x 1.6 mm, 14 faces (baked)
FEATURE [App::Part] LTC5548_1  label="LTC5548 1"
  Group = -> [_42_1701_626002,_42_1701_626003,_32147_48001,_42_1701_626004,_42_1701_626005,Part__Feature032]
  Origin = -> Origin038
  Placement = pos=(11,-11,0) rot=(0,0,1;0rad)
FEATURE [PartDesign::Boolean] Boolean010
  BaseFeature = -> Pocket008
  Group = -> [ScrewTap026,ScrewTap027,ScrewTap028,ScrewTap029]
  Refine = true
  Type = 1
FEATURE [Part::FeaturePython] ScrewTap042  label="M3x20.0-ScrewTap029"  # Fasteners workbench fastener (typed FeaturePython)
  Placement = pos=(11,12,12) rot=(0,0,1;0rad)
  diameter = 4
  invert = false
  length = 20
  matchOuter = true
  offset = 0
  thread = true
FEATURE [Part::FeaturePython] ScrewTap043  label="M3x20.0-ScrewTap030"  # Fasteners workbench fastener (typed FeaturePython)
  Placement = pos=(11,-34,12) rot=(0,0,1;0rad)
  diameter = 4
  invert = false
  length = 20
  matchOuter = true
  offset = 0
  thread = true
FEATURE [Part::FeaturePython] ScrewTap044  label="M3x20.0-ScrewTap031"  # Fasteners workbench fastener (typed FeaturePython)
  Placement = pos=(-0.5,-34,12) rot=(0,0,1;0rad)
  diameter = 4
  invert = false
  length = 20
  matchOuter = true
  offset = 0
  thread = true
FEATURE [Part::FeaturePython] ScrewTap045  label="M3x20.0-ScrewTap032"  # Fasteners workbench fastener (typed FeaturePython)
  Placement = pos=(-0.5,12,12) rot=(0,0,1;0rad)
  diameter = 4
  invert = false
  length = 20
  matchOuter = true
  offset = 0
  thread = true
FEATURE [Part::FeaturePython] ScrewTap046  label="M3x20.0-ScrewTap033"  # Fasteners workbench fastener (typed FeaturePython)
  Placement = pos=(22.5,12,12) rot=(0,0,1;0rad)
  diameter = 4
  invert = false
  length = 20
  matchOuter = true
  offset = 0
  thread = true
FEATURE [Part::FeaturePython] ScrewTap047  label="M3x20.0-ScrewTap034"  # Fasteners workbench fastener (typed FeaturePython)
  Placement = pos=(22.5,-34,12) rot=(0,0,1;0rad)
  diameter = 4
  invert = false
  length = 20
  matchOuter = true
  offset = 0
  thread = true
FEATURE [Part::FeaturePython] ScrewTap048  label="M3x20.0-ScrewTap040"  # Fasteners workbench fastener (typed FeaturePython)
  Placement = pos=(-12,-22.5,12) rot=(0,0,1;0rad)
  diameter = 4
  invert = false
  length = 20
  matchOuter = true
  offset = 0
  thread = true
FEATURE [Part::FeaturePython] ScrewTap049  label="M3x20.0-ScrewTap036"  # Fasteners workbench fastener (typed FeaturePython)
  Placement = pos=(34,-11,12) rot=(0,0,1;0rad)
  diameter = 4
  invert = false
  length = 20
  matchOuter = true
  offset = 0
  thread = true
FEATURE [Part::FeaturePython] ScrewTap050  label="M3x20.0-ScrewTap037"  # Fasteners workbench fastener (typed FeaturePython)
  Placement = pos=(34,0.5,12) rot=(0,0,1;0rad)
  diameter = 4
  invert = false
  length = 20
  matchOuter = true
  offset = 0
  thread = true
FEATURE [Part::FeaturePython] ScrewTap051  label="M3x20.0-ScrewTap038"  # Fasteners workbench fastener (typed FeaturePython)
  Placement = pos=(-12,0.5,12) rot=(0,0,1;0rad)
  diameter = 4
  invert = false
  length = 20
  matchOuter = true
  offset = 0
  thread = true
FEATURE [Part::FeaturePython] ScrewTap052  label="M3x20.0-ScrewTap039"  # Fasteners workbench fastener (typed FeaturePython)
  Placement = pos=(34,-22.5,12) rot=(0,0,1;0rad)
  diameter = 4
  invert = false
  length = 20
  matchOuter = true
  offset = 0
  thread = true
FEATURE [Part::FeaturePython] ScrewTap053  label="M3x20.0-ScrewTap041"  # Fasteners workbench fastener (typed FeaturePython)
  Placement = pos=(-12,-11,12) rot=(0,0,1;0rad)
  diameter = 4
  invert = false
  length = 20
  matchOuter = true
  offset = 0
  thread = true
FEATURE [Part::FeaturePython] ScrewTap054  label="M3x20.0-ScrewTap042"  # Fasteners workbench fastener (typed FeaturePython)
  Placement = pos=(11,12,12) rot=(0,0,1;0rad)
  diameter = 4
  invert = false
  length = 20
  matchOuter = true
  offset = 0
  thread = true
FEATURE [Part::FeaturePython] ScrewTap055  label="M3x20.0-ScrewTap043"  # Fasteners workbench fastener (typed FeaturePython)
  Placement = pos=(11,-34,12) rot=(0,0,1;0rad)
  diameter = 4
  invert = false
  length = 20
  matchOuter = true
  offset = 0
  thread = true
FEATURE [Part::FeaturePython] ScrewTap056  label="M3x20.0-ScrewTap044"  # Fasteners workbench fastener (typed FeaturePython)
  Placement = pos=(-0.5,-34,12) rot=(0,0,1;0rad)
  diameter = 4
  invert = false
  length = 20
  matchOuter = true
  offset = 0
  thread = true
FEATURE [Part::FeaturePython] ScrewTap057  label="M3x20.0-ScrewTap045"  # Fasteners workbench fastener (typed FeaturePython)
  Placement = pos=(-0.5,12,12) rot=(0,0,1;0rad)
  diameter = 4
  invert = false
  length = 20
  matchOuter = true
  offset = 0
  thread = true
FEATURE [Part::FeaturePython] ScrewTap058  label="M3x20.0-ScrewTap046"  # Fasteners workbench fastener (typed FeaturePython)
  Placement = pos=(22.5,12,12) rot=(0,0,1;0rad)
  diameter = 4
  invert = false
  length = 20
  matchOuter = true
  offset = 0
  thread = true
FEATURE [Part::FeaturePython] ScrewTap059  label="M3x20.0-ScrewTap047"  # Fasteners workbench fastener (typed FeaturePython)
  Placement = pos=(22.5,-34,12) rot=(0,0,1;0rad)
  diameter = 4
  invert = false
  length = 20
  matchOuter = true
  offset = 0
  thread = true
FEATURE [Part::FeaturePython] ScrewTap060  label="M3x20.0-ScrewTap048"  # Fasteners workbench fastener (typed FeaturePython)
  Placement = pos=(-12,-22.5,12) rot=(0,0,1;0rad)
  diameter = 4
  invert = false
  length = 20
  matchOuter = true
  offset = 0
  thread = true
FEATURE [Part::FeaturePython] ScrewTap061  label="M3x20.0-ScrewTap049"  # Fasteners workbench fastener (typed FeaturePython)
  Placement = pos=(34,-11,12) rot=(0,0,1;0rad)
  diameter = 4
  invert = false
  length = 20
  matchOuter = true
  offset = 0
  thread = true
FEATURE [Part::FeaturePython] ScrewTap062  label="M3x20.0-ScrewTap050"  # Fasteners workbench fastener (typed FeaturePython)
  Placement = pos=(34,0.5,12) rot=(0,0,1;0rad)
  diameter = 4
  invert = false
  length = 20
  matchOuter = true
  offset = 0
  thread = true
FEATURE [Part::FeaturePython] ScrewTap063  label="M3x20.0-ScrewTap051"  # Fasteners workbench fastener (typed FeaturePython)
  Placement = pos=(-12,0.5,12) rot=(0,0,1;0rad)
  diameter = 4
  invert = false
  length = 20
  matchOuter = true
  offset = 0
  thread = true
FEATURE [Part::FeaturePython] ScrewTap064  label="M3x20.0-ScrewTap052"  # Fasteners workbench fastener (typed FeaturePython)
  Placement = pos=(34,-22.5,12) rot=(0,0,1;0rad)
  diameter = 4
  invert = false
  length = 20
  matchOuter = true
  offset = 0
  thread = true
FEATURE [Part::FeaturePython] ScrewTap065  label="M3x20.0-ScrewTap053"  # Fasteners workbench fastener (typed FeaturePython)
  Placement = pos=(-12,-11,12) rot=(0,0,1;0rad)
  diameter = 4
  invert = false
  length = 20
  matchOuter = true
  offset = 0
  thread = true
FEATURE [PartDesign::Boolean] Boolean011
  BaseFeature = -> Pocket004
  Group = -> [ScrewTap054,ScrewTap055,ScrewTap056,ScrewTap057,ScrewTap058,ScrewTap059,ScrewTap060,ScrewTap061,ScrewTap062,ScrewTap063,ScrewTap064,ScrewTap065]
  Type = 1
FEATURE [PartDesign::Body] Body  label="Base"
  Group = -> [Sketch,Sketch006,Pad,Pad001,Sketch007,Pad002,Sketch008,Pocket,Boolean,Boolean001,Boolean002,Boolean003,Boolean004,Sketch009,Pocket001,Sketch010,Pocket002,Sketch011,Pocket003,Sketch012,Pocket004,Boolean011]
  Origin = -> Origin023
  Tip = -> Boolean011
FEATURE [App::Part] Part  label="3RF-1DC"
  Group = -> [Body]
  Origin = -> Origin024
FEATURE [PartDesign::Boolean] Boolean012
  BaseFeature = -> Boolean010
  Group = -> [ScrewTap042,ScrewTap043,ScrewTap044,ScrewTap045,ScrewTap046,ScrewTap047,ScrewTap048,ScrewTap049,ScrewTap050,ScrewTap051,ScrewTap052,ScrewTap053]
  Type = 1
FEATURE [PartDesign::Body] Body002  label="Base001"
  Group = -> [Sketch018,Sketch017,Pad005,Pad006,Sketch019,Pad007,Sketch020,Pocket005,Boolean005,Boolean006,Boolean007,Boolean008,Boolean009,Sketch021,Pocket006,Sketch023,Pocket009,Sketch022,Pocket007,Sketch024,Pocket008,Boolean010,Boolean012]
  Origin = -> Origin027
  Tip = -> Boolean012
FEATURE [App::Part] Part002  label="4RF-1DC"
  Group = -> [Body002]
  Origin = -> Origin028
